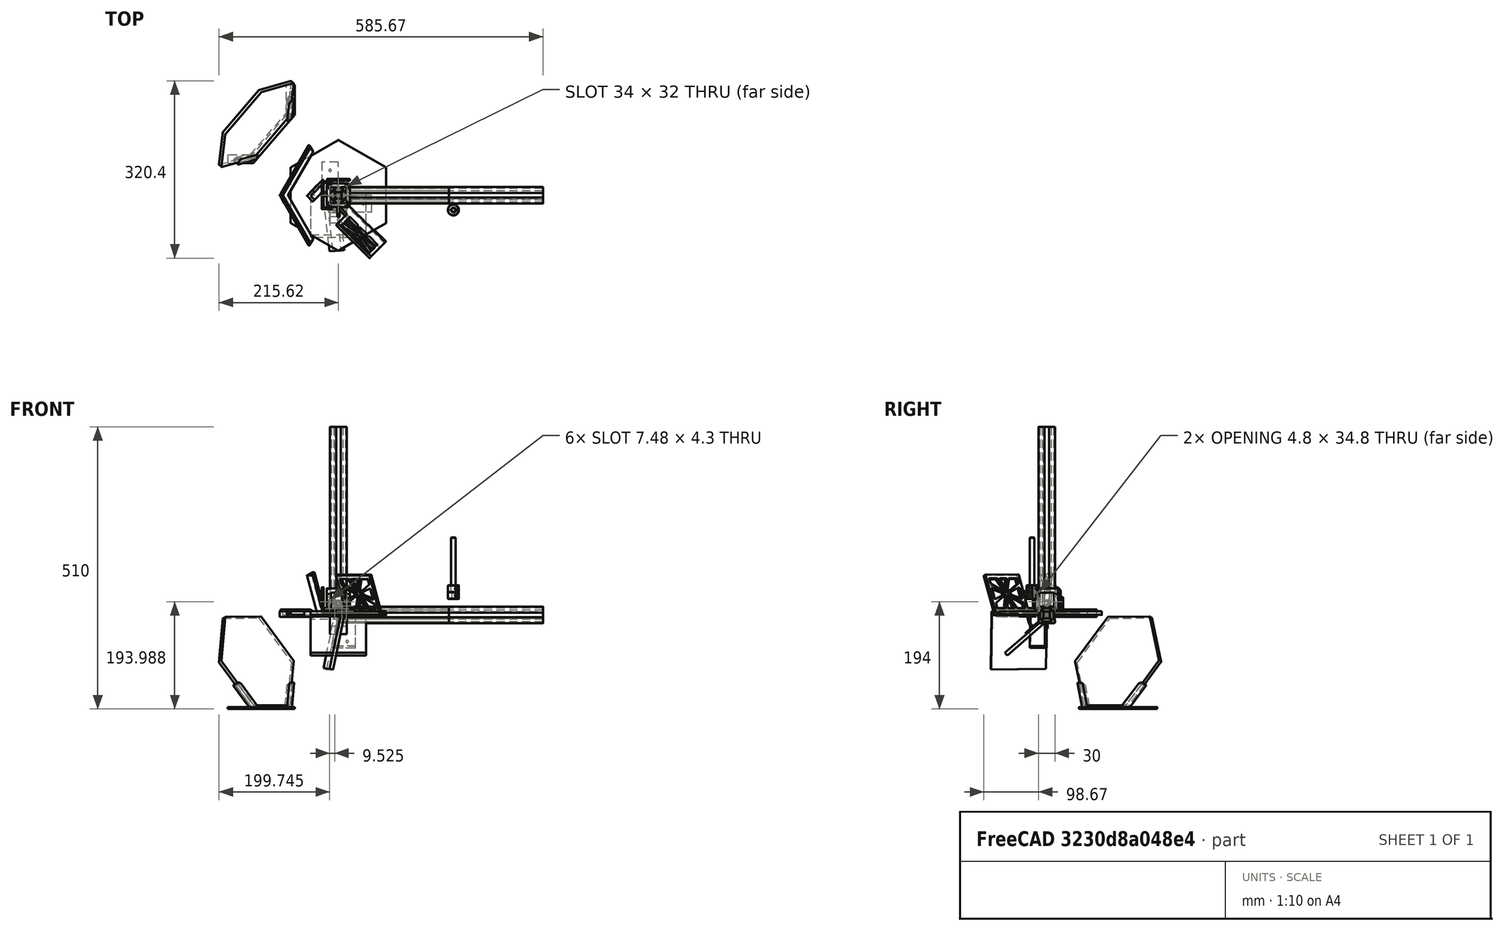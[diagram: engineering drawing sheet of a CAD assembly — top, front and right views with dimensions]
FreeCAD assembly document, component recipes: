
FREECAD ASSEMBLY — COMPONENT RECIPES ("frame")

This assembly document has 14 components, labeled P0..P13 below (a component is one placed body or linked part). 6 of them carry a construction recipe — the FreeCAD feature program that regenerates the part from scratch, quoted from this document or its linked companion documents; the rest are supplied as boundary geometry only. No exploded tour is included for this assembly.
COMPONENT P0 — geometry summary ("Extrusion"; no construction recipe available for this part):
  bounding box: 200.0 x 30.0 x 30.0 mm
  tessellated surface: 1,244 triangles
  volume: 87146 mm^3 (48% of its bounding box)
  symmetry: 4-fold rotationally symmetric about the x axis; 2-fold rotationally symmetric about the y axis; 2-fold rotationally symmetric about the z axis; mirror-symmetric across its x mid-plane, y mid-plane, z mid-plane
COMPONENT P1 — geometry summary ("Rubik's Cube"; no construction recipe available for this part):
  bounding box: 55.9 x 55.9 x 55.9 mm
  tessellated surface: 12 triangles
  volume: 174489 mm^3 (100% of its bounding box)
  symmetry: 4-fold rotationally symmetric about the x axis; 4-fold rotationally symmetric about the y axis; 4-fold rotationally symmetric about the z axis; mirror-symmetric across its x mid-plane, y mid-plane, z mid-plane
COMPONENT P2 — geometry summary ("Frame"; no construction recipe available for this part):
  bounding box: 503.7 x 446.7 x 440.0 mm
  tessellated surface: 211,220 triangles
  volume: 3022146 mm^3 (3% of its bounding box)
COMPONENT P3 — geometry summary ("Motor mount"; no construction recipe available for this part):
  bounding box: 74.0 x 64.2 x 51.2 mm
  tessellated surface: 18,230 triangles
  volume: 96011 mm^3 (40% of its bounding box)
COMPONENT P4 — geometry summary ("Extrusion 3"; no construction recipe available for this part):
  bounding box: 370.0 x 30.0 x 30.0 mm
  tessellated surface: 1,244 triangles
  volume: 161220 mm^3 (48% of its bounding box)
  symmetry: 4-fold rotationally symmetric about the x axis; 2-fold rotationally symmetric about the y axis; 2-fold rotationally symmetric about the z axis; mirror-symmetric across its x mid-plane, y mid-plane, z mid-plane
COMPONENT P5 — geometry summary ("Extrusion 2"; no construction recipe available for this part):
  bounding box: 200.0 x 30.0 x 30.0 mm
  tessellated surface: 1,244 triangles
  volume: 87146 mm^3 (48% of its bounding box)
  symmetry: 4-fold rotationally symmetric about the x axis; 2-fold rotationally symmetric about the y axis; 2-fold rotationally symmetric about the z axis; mirror-symmetric across its x mid-plane, y mid-plane, z mid-plane
COMPONENT P6 — geometry summary ("Extrusion 4"; no construction recipe available for this part):
  bounding box: 340.0 x 30.0 x 30.0 mm
  tessellated surface: 1,244 triangles
  volume: 148148 mm^3 (48% of its bounding box)
  symmetry: 2-fold rotationally symmetric about the x axis; 2-fold rotationally symmetric about the y axis; 4-fold rotationally symmetric about the z axis; mirror-symmetric across its x mid-plane, y mid-plane, z mid-plane
COMPONENT P7 — geometry summary ("Gripper"; no construction recipe available for this part):
  bounding box: 120.1 x 20.0 x 20.0 mm
  tessellated surface: 12,940 triangles
  volume: 14795 mm^3 (31% of its bounding box)
COMPONENT P8 — recipe-attached ("Mirror", modeled in this document).
Construction recipe (the document's own serialized feature program — sketch geometry with constraints, then the solid features built on it; lengths are millimeters unless a unit is written):

FEATURE [Sketcher::SketchObject] Sketch
  ArcFitTolerance = 1e-06
  AttachmentSupport = -> [XY_Plane011]
  ExternalTypes = [0]
  FullyConstrained = true
  MakeInternals = false
  MapMode = 5
  _ExternalGeoVersion = 0
  expr: Constraints[19] = Spreadsheet.H7
  sketch-geometry (7):
    g0: LineSegment StartX=-50 StartY=86.6025 StartZ=0 EndX=-100 EndY=0 EndZ=0
    g1: LineSegment StartX=-100 StartY=0 StartZ=0 EndX=-50 EndY=-86.6025 EndZ=0
    g2: LineSegment StartX=-50 StartY=-86.6025 StartZ=0 EndX=50 EndY=-86.6025 EndZ=0
    g3: LineSegment StartX=50 StartY=-86.6025 StartZ=0 EndX=100 EndY=-1.42e-14 EndZ=0
    g4: LineSegment StartX=100 StartY=-1.42e-14 StartZ=0 EndX=50 EndY=86.6025 EndZ=0
    g5: LineSegment StartX=50 StartY=86.6025 StartZ=0 EndX=-50 EndY=86.6025 EndZ=0
    g6: Circle [constr] CenterX=0 CenterY=0 CenterZ=0 NormalX=0 NormalY=0 NormalZ=1 AngleXU=0 Radius=100
  constraints (16):
    c: Coincident(g0,g1)
    c: Coincident(g1,g2)
    c: Coincident(g2,g3)
    c: Coincident(g3,g4)
    c: Coincident(g4,g5)
    c: Coincident(g5,g0)
    c: Equal(g0, g1-g5) x5
    c: PointOnObject(g0,g6)
    c: PointOnObject(g1,g6)
    c: PointOnObject(g2,g6)
    c: PointOnObject(g3,g6)
    c: PointOnObject(g4,g6)
    c: PointOnObject(g5,g6)
    c: Coincident(g6,g-1)
    c: Horizontal(g5)
    c: Diameter(g6) = 200
FEATURE [PartDesign::Pad] Pad001
  Direction = (0,0,1)
  Length = 6.35
  Length2 = 10
  Profile = -> Sketch
  ReferenceAxis = -> Sketch [N_Axis]
  Refine = true
  SideType = 0
  Suppressed = false
  Type = 0
  Type2 = 0
  expr: Length = Spreadsheet.H1
FEATURE [PartDesign::Fillet] Fillet001
  Base = -> Pad001 [Edge5,Edge8,Edge11,Edge14,Edge2,Edge1]
  BaseFeature = -> Pad001
  Radius = 1
  Refine = true
  SupportTransform = false
  Suppressed = false
  UseAllEdges = false
FEATURE [PartDesign::Body] Body001
  AllowCompound = false
  Group = -> [Pad001,Sketch,Fillet001]
  Origin = -> Origin011
  Placement = pos=(0,0,0) rot=(0,0,1;0.523599rad)
  Tip = -> Fillet001
COMPONENT P9 — recipe-attached ("Mirror frame", modeled in this document).
Construction recipe (the document's own serialized feature program — sketch geometry with constraints, then the solid features built on it; lengths are millimeters unless a unit is written):

FEATURE [Sketcher::SketchObject] Sketch002
  ArcFitTolerance = 1e-06
  AttachmentSupport = -> [XY_Plane013]
  ExternalTypes = [0]
  FullyConstrained = true
  MakeInternals = false
  MapMode = 5
  _ExternalGeoVersion = 0
  expr: Constraints[19] = Spreadsheet.H7 + Spreadsheet.H6
  expr: Constraints[34] = Spreadsheet.H3
  sketch-geometry (13):
    g0: LineSegment [constr] StartX=50.125 StartY=-86.819 StartZ=0 EndX=100.25 EndY=-5.684e-13 EndZ=0
    g1: LineSegment [constr] StartX=100.25 StartY=-5.684e-13 StartZ=0 EndX=50.125 EndY=86.819 EndZ=0
    g2: LineSegment [constr] StartX=50.125 StartY=86.819 StartZ=0 EndX=-50.125 EndY=86.819 EndZ=0
    g3: LineSegment StartX=-50.125 StartY=86.819 StartZ=0 EndX=-100.25 EndY=1.99e-13 EndZ=0
    g4: LineSegment StartX=-100.25 StartY=1.99e-13 StartZ=0 EndX=-50.125 EndY=-86.819 EndZ=0
    g5: LineSegment [constr] StartX=-50.125 StartY=-86.819 StartZ=0 EndX=50.125 EndY=-86.819 EndZ=0
    g6: Circle [constr] CenterX=0 CenterY=0 CenterZ=0 NormalX=0 NormalY=0 NormalZ=1 AngleXU=0 Radius=100.25
    g7: LineSegment [constr] StartX=0 StartY=0 StartZ=0 EndX=-50.125 EndY=86.819 EndZ=0
    g8: LineSegment [constr] StartX=0 StartY=0 StartZ=0 EndX=-50.125 EndY=-86.819 EndZ=0
    g9: LineSegment StartX=-50.125 StartY=-86.819 StartZ=0 EndX=-45.5062 EndY=-78.819 EndZ=0
    g10: LineSegment StartX=-50.125 StartY=86.819 StartZ=0 EndX=-45.5062 EndY=78.819 EndZ=0
    g11: LineSegment StartX=-45.5062 StartY=78.819 StartZ=0 EndX=-91.0124 EndY=0 EndZ=0
    g12: LineSegment StartX=-91.0124 StartY=0 StartZ=0 EndX=-45.5062 EndY=-78.819 EndZ=0
  constraints (31):
    c: Coincident(g0,g1)
    c: Coincident(g1,g2)
    c: Coincident(g2,g3)
    c: Coincident(g3,g4)
    c: Coincident(g4,g5)
    c: Coincident(g5,g0)
    c: Equal(g0, g1-g5) x5
    c: PointOnObject(g0,g6)
    c: PointOnObject(g1,g6)
    c: PointOnObject(g2,g6)
    c: PointOnObject(g3,g6)
    c: PointOnObject(g4,g6)
    c: PointOnObject(g5,g6)
    c: Coincident(g6,g-1)
    c: Horizontal(g2)
    c: DistanceX(g3,g0) = 200.5
    c: Coincident(g7,g6)
    c: Coincident(g7,g2)
    c: Coincident(g8,g6)
    c: Coincident(g8,g4)
    c: Coincident(g9,g4)
    c: PointOnObject(g9,g8)
    c: Coincident(g10,g2)
    c: PointOnObject(g10,g7)
    c: Coincident(g11,g10)
    c: PointOnObject(g11,g-1)
    c: Coincident(g12,g11)
    c: Coincident(g12,g9)
    c: Parallel(g3,g11)
    c: Parallel(g12,g4)
    c: Distance(g11,g3) = 8
FEATURE [PartDesign::Pad] Pad002
  Direction = (0,0,1)
  Length = 3
  Length2 = 10
  Profile = -> Sketch002
  ReferenceAxis = -> Sketch002 [N_Axis]
  Refine = true
  SideType = 0
  Suppressed = false
  Type = 0
  Type2 = 0
  expr: Length = Spreadsheet.H2
FEATURE [Sketcher::SketchObject] Sketch003  label="Sketch006"
  ArcFitTolerance = 1e-06
  AttachmentSupport = -> [XY_Plane013]
  ExternalTypes = [0]
  FullyConstrained = true
  MakeInternals = false
  MapMode = 5
  _ExternalGeoVersion = 0
  expr: Constraints[19] = Spreadsheet.H7 + Spreadsheet.H6
  expr: Constraints[34] = Spreadsheet.H4
  sketch-geometry (13):
    g0: LineSegment [constr] StartX=50.125 StartY=-86.819 StartZ=0 EndX=100.25 EndY=-5.542e-13 EndZ=0
    g1: LineSegment [constr] StartX=100.25 StartY=-5.542e-13 StartZ=0 EndX=50.125 EndY=86.819 EndZ=0
    g2: LineSegment [constr] StartX=50.125 StartY=86.819 StartZ=0 EndX=-50.125 EndY=86.819 EndZ=0
    g3: LineSegment StartX=-50.125 StartY=86.819 StartZ=0 EndX=-100.25 EndY=1.705e-13 EndZ=0
    g4: LineSegment StartX=-100.25 StartY=1.705e-13 StartZ=0 EndX=-50.125 EndY=-86.819 EndZ=0
    g5: LineSegment [constr] StartX=-50.125 StartY=-86.819 StartZ=0 EndX=50.125 EndY=-86.819 EndZ=0
    g6: Circle [constr] CenterX=0 CenterY=0 CenterZ=0 NormalX=0 NormalY=0 NormalZ=1 AngleXU=0 Radius=100.25
    g7: LineSegment [constr] StartX=0 StartY=0 StartZ=0 EndX=-50.125 EndY=86.819 EndZ=0
    g8: LineSegment [constr] StartX=0 StartY=0 StartZ=0 EndX=-50.125 EndY=-86.819 EndZ=0
    g9: LineSegment StartX=-50.125 StartY=-86.819 StartZ=0 EndX=-53.0118 EndY=-91.819 EndZ=0
    g10: LineSegment StartX=-50.125 StartY=86.819 StartZ=0 EndX=-53.0118 EndY=91.819 EndZ=0
    g11: LineSegment StartX=-53.0118 StartY=91.819 StartZ=0 EndX=-106.024 EndY=0 EndZ=0
    g12: LineSegment StartX=-106.024 StartY=0 StartZ=0 EndX=-53.0118 EndY=-91.819 EndZ=0
  constraints (31):
    c: Coincident(g0,g1)
    c: Coincident(g1,g2)
    c: Coincident(g2,g3)
    c: Coincident(g3,g4)
    c: Coincident(g4,g5)
    c: Coincident(g5,g0)
    c: Equal(g0, g1-g5) x5
    c: PointOnObject(g0,g6)
    c: PointOnObject(g1,g6)
    c: PointOnObject(g2,g6)
    c: PointOnObject(g3,g6)
    c: PointOnObject(g4,g6)
    c: PointOnObject(g5,g6)
    c: Coincident(g6,g-1)
    c: Horizontal(g2)
    c: DistanceX(g3,g0) = 200.5
    c: Coincident(g7,g6)
    c: Coincident(g7,g2)
    c: Coincident(g8,g6)
    c: Coincident(g8,g4)
    c: Coincident(g9,g4)
    c: PointOnObject(g9,g8)
    c: Coincident(g10,g2)
    c: PointOnObject(g10,g7)
    c: Coincident(g11,g10)
    c: PointOnObject(g11,g-1)
    c: Coincident(g12,g11)
    c: Coincident(g12,g9)
    c: Parallel(g3,g11)
    c: Parallel(g12,g4)
    c: Distance(g3,g11) = 5
FEATURE [PartDesign::Pad] Pad003
  BaseFeature = -> Pad002
  Direction = (0,0,1)
  Length = 10.35
  Length2 = 10
  Profile = -> Sketch003
  ReferenceAxis = -> Sketch003 [N_Axis]
  Refine = true
  SideType = 0
  Suppressed = false
  Type = 0
  Type2 = 0
  expr: Length = Spreadsheet.H5
FEATURE [Sketcher::SketchObject] Sketch004  label="Sketch007"
  ArcFitTolerance = 1e-06
  AttachmentSupport = -> [XZ_Plane014]
  ExternalTypes = [0]
  FullyConstrained = true
  MakeInternals = false
  MapMode = 5
  Placement = pos=(0,0,0) rot=(1,0,0;1.5708rad)
  _ExternalGeoVersion = 0
  expr: Constraints[16] = Spreadsheet.H9
  expr: Constraints[17] = Spreadsheet.H12
  expr: Constraints[18] = Spreadsheet.H1 + Spreadsheet.H6
  expr: Constraints[7] = Spreadsheet.H10 / 2
  expr: Constraints[9] = Spreadsheet.H11
  sketch-geometry (7):
    g0: LineSegment StartX=-103.5 StartY=6.85 StartZ=0 EndX=-104 EndY=8.35 EndZ=0
    g1: LineSegment StartX=-104 StartY=8.35 StartZ=0 EndX=-103.5 EndY=9.85 EndZ=0
    g2: LineSegment StartX=-103.5 StartY=9.85 StartZ=0 EndX=-101.5 EndY=9.85 EndZ=0
    g3: LineSegment StartX=-101.5 StartY=9.85 StartZ=0 EndX=-101 EndY=8.35 EndZ=0
    g4: LineSegment StartX=-101 StartY=8.35 StartZ=0 EndX=-101.5 EndY=6.85 EndZ=0
    g5: LineSegment StartX=-101.5 StartY=6.85 StartZ=0 EndX=-103.5 EndY=6.85 EndZ=0
    g6: LineSegment [constr] StartX=-102.5 StartY=9.85 StartZ=0 EndX=-102.5 EndY=6.85 EndZ=0
  constraints (19):
    c: Coincident(g1,g0)
    c: Coincident(g2,g1)
    c: Coincident(g3,g2)
    c: Coincident(g5,g4)
    c: Coincident(g5,g0)
    c: Equal(g2,g5)
    c: Coincident(g3,g4)
    c: DistanceX(g0,g1) = 0.5
    c: Equal(g1,g0)
    c: DistanceX(g0,g3) = 3
    c: PointOnObject(g6,g2)
    c: Symmetric(g5,g5,g6)
    c: Vertical(g6)
    c: Symmetric(g1,g2,g6)
    c: Symmetric(g0,g3,g6)
    c: Horizontal(g5)
    c: DistanceY(g6,g6) = 3
    c: Distance(g-1,g6) = 102.5
    c: Distance(g-1,g5) = 6.85
FEATURE [Sketcher::SketchObject] Sketch005  label="Sketch008"
  ArcFitTolerance = 1e-06
  AttachmentSupport = -> [XY_Plane014]
  ExternalTypes = [0]
  FullyConstrained = true
  MakeInternals = false
  MapMode = 5
  _ExternalGeoVersion = 0
  expr: Constraints[4] = Spreadsheet.H7 / 1.5
  sketch-geometry (2):
    g0: LineSegment StartX=0 StartY=0 StartZ=0 EndX=66.6667 EndY=115.47 EndZ=0
    g1: LineSegment StartX=0 StartY=0 StartZ=0 EndX=66.6667 EndY=-115.47 EndZ=0
  constraints (5):
    c: Coincident(g0,g-1)
    c: Coincident(g1,g0)
    c: Symmetric(g0,g1,g-1)
    c: Angle(g1,g0) = 2.0944
    c: Distance(g1,g1) = 133.333
FEATURE [PartDesign::AdditivePipe] AdditivePipe
  AuxiliaryCurvilinear = true
  AuxiliarySpineTangent = false
  Binormal = (0,0,0)
  Mode = 0
  Placement = pos=(0,0,0) rot=(1,0,0;1.5708rad)
  Profile = -> Sketch004
  Refine = true
  Spine = -> Sketch005
  SpineTangent = false
  Suppressed = false
  Transformation = 0
  Transition = 0
FEATURE [Sketcher::SketchObject] Sketch006  label="Sketch009"
  ArcFitTolerance = 1e-06
  AttachmentSupport = -> [XY_Plane014]
  ExternalTypes = [0]
  FullyConstrained = true
  MakeInternals = false
  MapMode = 5
  _ExternalGeoVersion = 0
  expr: Constraints[18] = Spreadsheet.H7 * 1.5
  expr: Constraints[34] = Spreadsheet.H7
  sketch-geometry (13):
    g0: LineSegment [constr] StartX=75 StartY=-129.904 StartZ=0 EndX=150 EndY=0 EndZ=0
    g1: LineSegment [constr] StartX=150 StartY=0 StartZ=0 EndX=75 EndY=129.904 EndZ=0
    g2: LineSegment [constr] StartX=75 StartY=129.904 StartZ=0 EndX=-75 EndY=129.904 EndZ=0
    g3: LineSegment [constr] StartX=-75 StartY=129.904 StartZ=0 EndX=-150 EndY=-2.84e-14 EndZ=0
    g4: LineSegment [constr] StartX=-150 StartY=-2.84e-14 StartZ=0 EndX=-75 EndY=-129.904 EndZ=0
    g5: LineSegment [constr] StartX=-75 StartY=-129.904 StartZ=0 EndX=75 EndY=-129.904 EndZ=0
    g6: Circle [constr] CenterX=0 CenterY=0 CenterZ=0 NormalX=0 NormalY=0 NormalZ=1 AngleXU=0 Radius=150
    g7: LineSegment StartX=0 StartY=0 StartZ=0 EndX=-115.47 EndY=200 EndZ=0
    g8: LineSegment StartX=0 StartY=0 StartZ=0 EndX=-115.47 EndY=-200 EndZ=0
    g9: LineSegment StartX=-115.47 StartY=-200 StartZ=0 EndX=34.5299 EndY=-200 EndZ=0
    g10: LineSegment StartX=34.5299 StartY=-200 StartZ=0 EndX=150 EndY=0 EndZ=0
    g11: LineSegment StartX=-115.47 StartY=200 StartZ=0 EndX=34.5299 EndY=200 EndZ=0
    g12: LineSegment StartX=34.5299 StartY=200 StartZ=0 EndX=150 EndY=0 EndZ=0
  constraints (31):
    c: Coincident(g0,g1)
    c: Coincident(g1,g2)
    c: Coincident(g2,g3)
    c: Coincident(g3,g4)
    c: Coincident(g4,g5)
    c: Coincident(g5,g0)
    c: Equal(g0, g1-g5) x5
    c: PointOnObject(g0,g6)
    c: PointOnObject(g1,g6)
    c: PointOnObject(g3,g6)
    c: PointOnObject(g4,g6)
    c: PointOnObject(g5,g6)
    c: Coincident(g6,g-1)
    c: Horizontal(g2)
    c: Diameter(g6) = 300
    c: Coincident(g7,g6)
    c: Coincident(g8,g6)
    c: PointOnObject(g2,g7)
    c: PointOnObject(g2,g6)
    c: Coincident(g9,g8)
    c: Coincident(g10,g9)
    c: Coincident(g10,g0)
    c: Coincident(g12,g11)
    c: Coincident(g12,g0)
    c: Horizontal(g11)
    c: Horizontal(g9)
    c: Coincident(g11,g7)
    c: Parallel(g7,g12)
    c: Parallel(g8,g10)
    c: Symmetric(g7,g8,g-1)
    c: DistanceY(g7,g7) = 200
FEATURE [PartDesign::Pocket] Pocket
  BaseFeature = -> AdditivePipe
  Direction = (0,0,-1)
  Length = 100
  Length2 = 5
  Placement = pos=(0,0,0) rot=(1,0,0;1.5708rad)
  Profile = -> Sketch006
  ReferenceAxis = -> Sketch006 [N_Axis]
  Refine = true
  Reversed = true
  SideType = 0
  Suppressed = false
  Type = 0
  Type2 = 0
FEATURE [PartDesign::Fillet] Fillet002
  Base = -> Pocket [Edge12,Edge2,Edge28,Edge19]
  BaseFeature = -> Pocket
  Placement = pos=(0,0,0) rot=(1,0,0;1.5708rad)
  Radius = 1
  Refine = true
  SupportTransform = false
  Suppressed = false
  UseAllEdges = false
FEATURE [PartDesign::Body] Body003
  AllowCompound = false
  Group = -> [Sketch004,Sketch005,AdditivePipe,Sketch006,Pocket,Fillet002]
  Origin = -> Origin014
  Tip = -> Fillet002
FEATURE [PartDesign::Boolean] Boolean
  BaseFeature = -> Pad003
  Group = -> [Binder]
  Refine = true
  Suppressed = false
  Type = 0
FEATURE [Sketcher::SketchObject] Sketch007  label="Sketch010"
  ArcFitTolerance = 1e-06
  AttachmentSupport = -> [XY_Plane013]
  ExternalTypes = [0]
  FullyConstrained = true
  MakeInternals = false
  MapMode = 5
  _ExternalGeoVersion = 0
  expr: Constraints[19] = Spreadsheet.H7 + Spreadsheet.H6
  expr: Constraints[36] = Spreadsheet.H14
  expr: Constraints[37] = Spreadsheet.H14
  expr: Constraints[52] = Spreadsheet.H4
  sketch-geometry (19):
    g0: LineSegment [constr] StartX=50.125 StartY=86.819 StartZ=0 EndX=-50.125 EndY=86.819 EndZ=0
    g1: LineSegment [constr] StartX=-50.125 StartY=86.819 StartZ=0 EndX=-100.25 EndY=0 EndZ=0
    g2: LineSegment [constr] StartX=-100.25 StartY=0 StartZ=0 EndX=-50.125 EndY=-86.819 EndZ=0
    g3: LineSegment [constr] StartX=-50.125 StartY=-86.819 StartZ=0 EndX=50.125 EndY=-86.819 EndZ=0
    g4: LineSegment [constr] StartX=50.125 StartY=-86.819 StartZ=0 EndX=100.25 EndY=-1.42e-14 EndZ=0
    g5: LineSegment [constr] StartX=100.25 StartY=-1.42e-14 StartZ=0 EndX=50.125 EndY=86.819 EndZ=0
    g6: Circle [constr] CenterX=0 CenterY=0 CenterZ=0 NormalX=0 NormalY=0 NormalZ=1 AngleXU=0 Radius=100.25
    g7: LineSegment [constr] StartX=0 StartY=0 StartZ=0 EndX=-53.0118 EndY=91.819 EndZ=0
    g8: LineSegment [constr] StartX=1.588e-13 StartY=0 StartZ=0 EndX=-53.0118 EndY=-91.819 EndZ=0
    g9: LineSegment [constr] StartX=-53.0118 StartY=91.819 StartZ=0 EndX=-106.024 EndY=0 EndZ=0
    g10: LineSegment [constr] StartX=-106.024 StartY=0 StartZ=0 EndX=-53.0118 EndY=-91.819 EndZ=0
    g11: LineSegment StartX=-61.9551 StartY=76.3287 StartZ=0 EndX=-57.625 EndY=73.8287 EndZ=0
    g12: LineSegment StartX=-97.0801 StartY=15.4904 StartZ=0 EndX=-92.75 EndY=12.9904 EndZ=0
    g13: LineSegment StartX=-97.0801 StartY=-15.4904 StartZ=0 EndX=-92.75 EndY=-12.9904 EndZ=0
    g14: LineSegment StartX=-61.9551 StartY=-76.3287 StartZ=0 EndX=-57.625 EndY=-73.8287 EndZ=0
    g15: LineSegment StartX=-57.625 StartY=73.8287 StartZ=0 EndX=-92.75 EndY=12.9904 EndZ=0
    g16: LineSegment StartX=-97.0801 StartY=15.4904 StartZ=0 EndX=-61.9551 EndY=76.3287 EndZ=0
    g17: LineSegment StartX=-92.75 StartY=-12.9904 StartZ=0 EndX=-57.625 EndY=-73.8287 EndZ=0
    g18: LineSegment StartX=-61.9551 StartY=-76.3287 StartZ=0 EndX=-97.0801 EndY=-15.4904 EndZ=0
  constraints (49):
    c: Coincident(g0,g1)
    c: Coincident(g1,g2)
    c: Coincident(g2,g3)
    c: Coincident(g3,g4)
    c: Coincident(g4,g5)
    c: Coincident(g5,g0)
    c: Equal(g0, g1-g5) x5
    c: PointOnObject(g0,g6)
    c: PointOnObject(g1,g6)
    c: PointOnObject(g2,g6)
    c: PointOnObject(g3,g6)
    c: PointOnObject(g4,g6)
    c: PointOnObject(g5,g6)
    c: Coincident(g6,g-1)
    c: Horizontal(g0)
    c: Diameter(g6) = 200.5
    c: Coincident(g7,g6)
    c: PointOnObject(g8,g-1)
    c: PointOnObject(g2,g8)
    c: PointOnObject(g0,g7)
    c: Symmetric(g7,g8,g-1)
    c: Coincident(g9,g7)
    c: PointOnObject(g9,g-1)
    c: Coincident(g10,g9)
    c: Coincident(g10,g8)
    c: Parallel(g10,g2)
    c: PointOnObject(g11,g9)
    c: PointOnObject(g11,g1)
    c: PointOnObject(g12,g9)
    c: PointOnObject(g12,g1)
    c: Perpendicular(g11,g9)
    c: Perpendicular(g12,g9)
    c: Distance(g0,g11) = 15
    c: Distance(g12,g1) = 15
    c: PointOnObject(g13,g10)
    c: PointOnObject(g14,g10)
    c: Perpendicular(g13,g2)
    c: Perpendicular(g14,g2)
    c: Symmetric(g12,g13,g-1)
    c: Symmetric(g14,g11,g-1)
    c: Coincident(g15,g11)
    c: Coincident(g15,g12)
    c: Coincident(g16,g12)
    c: Coincident(g16,g11)
    c: Coincident(g17,g13)
    c: Coincident(g17,g14)
    c: Coincident(g18,g14)
    c: Coincident(g18,g13)
    c: Distance(g1,g9) = 5
FEATURE [PartDesign::Pocket] Pocket001
  BaseFeature = -> Boolean
  Direction = (0,0,-1)
  Length = 100
  Length2 = 5
  Profile = -> Sketch007
  ReferenceAxis = -> Sketch007 [N_Axis]
  Refine = true
  Reversed = true
  SideType = 0
  Suppressed = false
  Type = 0
  Type2 = 0
FEATURE [Sketcher::SketchObject] Sketch008  label="Sketch011"
  ArcFitTolerance = 1e-06
  AttachmentSupport = -> [XY_Plane013]
  ExternalTypes = [0]
  FullyConstrained = true
  MakeInternals = false
  MapMode = 5
  _ExternalGeoVersion = 0
  expr: Constraints[19] = Spreadsheet.H7 + Spreadsheet.H6
  expr: Constraints[23] = Spreadsheet.H4
  expr: Constraints[33] = Spreadsheet.H4
  expr: Constraints[34] = Spreadsheet.H19
  sketch-geometry (15):
    g0: LineSegment [constr] StartX=50.125 StartY=86.819 StartZ=0 EndX=-50.125 EndY=86.819 EndZ=0
    g1: LineSegment [constr] StartX=-50.125 StartY=86.819 StartZ=0 EndX=-100.25 EndY=0 EndZ=0
    g2: LineSegment [constr] StartX=-100.25 StartY=0 StartZ=0 EndX=-50.125 EndY=-86.819 EndZ=0
    g3: LineSegment [constr] StartX=-50.125 StartY=-86.819 StartZ=0 EndX=50.125 EndY=-86.819 EndZ=0
    g4: LineSegment [constr] StartX=50.125 StartY=-86.819 StartZ=0 EndX=100.25 EndY=0 EndZ=0
    g5: LineSegment [constr] StartX=100.25 StartY=0 StartZ=0 EndX=50.125 EndY=86.819 EndZ=0
    g6: Circle [constr] CenterX=0 CenterY=0 CenterZ=0 NormalX=0 NormalY=0 NormalZ=1 AngleXU=0 Radius=100.25
    g7: LineSegment StartX=-88.3301 StartY=-30.6458 StartZ=0 EndX=-90.8301 EndY=-26.3157 EndZ=0
    g8: LineSegment StartX=-90.8301 StartY=-26.3157 StartZ=0 EndX=-86.5 EndY=-23.8157 EndZ=0
    g9: LineSegment StartX=-86.5 StartY=23.8157 StartZ=0 EndX=-84 EndY=28.1458 EndZ=0
    g10: LineSegment StartX=-84 StartY=28.1458 StartZ=0 EndX=-88.3301 EndY=30.6458 EndZ=0
    g11: LineSegment StartX=-88.3301 StartY=30.6458 StartZ=0 EndX=-90.8301 EndY=26.3157 EndZ=0
    g12: LineSegment StartX=-90.8301 StartY=26.3157 StartZ=0 EndX=-86.5 EndY=23.8157 EndZ=0
    g13: LineSegment StartX=-86.5 StartY=-23.8157 StartZ=0 EndX=-84 EndY=-28.1458 EndZ=0
    g14: LineSegment StartX=-88.3301 StartY=-30.6458 StartZ=0 EndX=-84 EndY=-28.1458 EndZ=0
  constraints (39):
    c: Coincident(g0,g1)
    c: Coincident(g1,g2)
    c: Coincident(g2,g3)
    c: Coincident(g3,g4)
    c: Coincident(g4,g5)
    c: Coincident(g5,g0)
    c: Equal(g0, g1-g5) x5
    c: PointOnObject(g0,g6)
    c: PointOnObject(g1,g6)
    c: PointOnObject(g2,g6)
    c: PointOnObject(g3,g6)
    c: PointOnObject(g4,g6)
    c: PointOnObject(g5,g6)
    c: Coincident(g6,g-1)
    c: Horizontal(g0)
    c: Diameter(g6) = 200.5
    c: PointOnObject(g8,g2)
    c: Coincident(g8,g7)
    c: Equal(g8,g7)
    c: Distance(g8,g8) = 5
    c: PointOnObject(g9,g1)
    c: Coincident(g10,g9)
    c: Coincident(g11,g10)
    c: Coincident(g12,g11)
    c: Coincident(g12,g9)
    c: Perpendicular(g10,g11)
    c: Perpendicular(g12,g11)
    c: Equal(g11,g10)
    c: Equal(g11,g12)
    c: Distance(g10,g10) = 5
    c: Distance(g1,g8) = 27.5
    c: Coincident(g13,g8)
    c: Coincident(g14,g7)
    c: Coincident(g14,g13)
    c: PointOnObject(g13,g2)
    c: Equal(g13,g7)
    c: Equal(g8,g14)
    c: Perpendicular(g7,g8)
    c: Symmetric(g9,g8,g-1)
FEATURE [PartDesign::Pad] Pad004
  BaseFeature = -> Pocket001
  Direction = (0,0,1)
  Length = 10.35
  Length2 = 10
  Profile = -> Sketch008
  ReferenceAxis = -> Sketch008 [N_Axis]
  Refine = true
  SideType = 0
  Suppressed = false
  Type = 0
  Type2 = 0
  expr: Length = Spreadsheet.H5
FEATURE [Sketcher::SketchObject] Sketch009  label="Sketch012"
  ArcFitTolerance = 1e-06
  AttachmentSupport = -> [XY_Plane013]
  ExternalTypes = [0]
  FullyConstrained = true
  MakeInternals = false
  MapMode = 5
  _ExternalGeoVersion = 0
  expr: Constraints[1] = Spreadsheet.H20 - Spreadsheet.H21
  expr: Constraints[22] = Spreadsheet.H7 + Spreadsheet.H6
  expr: Constraints[26] = Spreadsheet.H4 / 2
  expr: Constraints[27] = Spreadsheet.H18
  sketch-geometry (10):
    g0: Circle CenterX=-87.4151 CenterY=27.2308 CenterZ=0 NormalX=0 NormalY=0 NormalZ=1 AngleXU=0 Radius=1.25
    g1: Circle CenterX=-87.4151 CenterY=-27.2308 CenterZ=0 NormalX=0 NormalY=0 NormalZ=1 AngleXU=0 Radius=1.25
    g2: LineSegment [constr] StartX=-50.125 StartY=86.819 StartZ=0 EndX=-100.25 EndY=0 EndZ=0
    g3: LineSegment [constr] StartX=-100.25 StartY=0 StartZ=0 EndX=-50.125 EndY=-86.819 EndZ=0
    g4: LineSegment [constr] StartX=-50.125 StartY=-86.819 StartZ=0 EndX=50.125 EndY=-86.819 EndZ=0
    g5: LineSegment [constr] StartX=50.125 StartY=-86.819 StartZ=0 EndX=100.25 EndY=0 EndZ=0
    g6: LineSegment [constr] StartX=100.25 StartY=0 StartZ=0 EndX=50.125 EndY=86.819 EndZ=0
    g7: LineSegment [constr] StartX=50.125 StartY=86.819 StartZ=0 EndX=-50.125 EndY=86.819 EndZ=0
    g8: Circle [constr] CenterX=0 CenterY=0 CenterZ=0 NormalX=0 NormalY=0 NormalZ=1 AngleXU=0 Radius=100.25
    g9: LineSegment [constr] StartX=-87.4151 StartY=-27.2308 StartZ=0 EndX=-85.25 EndY=-25.9808 EndZ=0
  constraints (24):
    c: Equal(g0,g1)
    c: Diameter(g0) = 2.5
    c: Symmetric(g0,g1,g-1)
    c: Coincident(g2,g3)
    c: Coincident(g3,g4)
    c: Coincident(g4,g5)
    c: Coincident(g5,g6)
    c: Coincident(g6,g7)
    c: Coincident(g7,g2)
    c: Equal(g2, g3-g7) x5
    c: PointOnObject(g2,g8)
    c: PointOnObject(g3,g8)
    c: PointOnObject(g4,g8)
    c: PointOnObject(g5,g8)
    c: PointOnObject(g6,g8)
    c: PointOnObject(g7,g8)
    c: Coincident(g8,g-1)
    c: Horizontal(g7)
    c: Diameter(g8) = 200.5
    c: Coincident(g9,g1)
    c: PointOnObject(g9,g3)
    c: Perpendicular(g9,g3)
    c: Distance(g9,g9) = 2.5
    c: Distance(g9,g2) = 30
FEATURE [PartDesign::Pad] Pad005
  BaseFeature = -> Pad004
  Direction = (0,0,1)
  Length = 13.35
  Length2 = 10
  Profile = -> Sketch009
  ReferenceAxis = -> Sketch009 [N_Axis]
  Refine = true
  SideType = 0
  Suppressed = false
  Type = 0
  Type2 = 0
  expr: Length = Spreadsheet.K9
FEATURE [PartDesign::Plane] DatumPlane
  Length = 160.897
  MapMode = 1
  Placement = pos=(0,0,6.85) rot=(0,0,1;0rad)
  ResizeMode = 0
  Width = 212.388
  expr: .Placement.Base.z = Spreadsheet.H5 - Spreadsheet.H2 - Spreadsheet.H6
FEATURE [Sketcher::SketchObject] Sketch010  label="Sketch013"
  ArcFitTolerance = 1e-06
  AttachmentSupport = -> [DatumPlane]
  ExternalTypes = [0]
  FullyConstrained = true
  MakeInternals = false
  MapMode = 5
  Placement = pos=(0,0,6.85) rot=(0,0,1;0rad)
  _ExternalGeoVersion = 0
  expr: Constraints[19] = Spreadsheet.H7 + Spreadsheet.H6
  expr: Constraints[28] = Spreadsheet.H4
  expr: Constraints[40] = Spreadsheet.H3
  sketch-geometry (15):
    g0: LineSegment [constr] StartX=50.125 StartY=86.819 StartZ=0 EndX=-50.125 EndY=86.819 EndZ=0
    g1: LineSegment [constr] StartX=-50.125 StartY=86.819 StartZ=0 EndX=-100.25 EndY=0 EndZ=0
    g2: LineSegment [constr] StartX=-100.25 StartY=0 StartZ=0 EndX=-50.125 EndY=-86.819 EndZ=0
    g3: LineSegment [constr] StartX=-50.125 StartY=-86.819 StartZ=0 EndX=50.125 EndY=-86.819 EndZ=0
    g4: LineSegment [constr] StartX=50.125 StartY=-86.819 StartZ=0 EndX=100.25 EndY=0 EndZ=0
    g5: LineSegment [constr] StartX=100.25 StartY=0 StartZ=0 EndX=50.125 EndY=86.819 EndZ=0
    g6: Circle [constr] CenterX=0 CenterY=0 CenterZ=0 NormalX=0 NormalY=0 NormalZ=1 AngleXU=0 Radius=100.25
    g7: LineSegment [constr] StartX=0 StartY=0 StartZ=0 EndX=-53.0118 EndY=91.819 EndZ=0
    g8: LineSegment [constr] StartX=0 StartY=0 StartZ=0 EndX=-53.0118 EndY=-91.819 EndZ=0
    g9: LineSegment StartX=-53.0118 StartY=-91.819 StartZ=0 EndX=-106.024 EndY=0 EndZ=0
    g10: LineSegment StartX=-106.024 StartY=0 StartZ=0 EndX=-53.0118 EndY=91.819 EndZ=0
    g11: LineSegment StartX=-53.0118 StartY=91.819 StartZ=0 EndX=-45.5062 EndY=78.819 EndZ=0
    g12: LineSegment StartX=-53.0118 StartY=-91.819 StartZ=0 EndX=-45.5062 EndY=-78.819 EndZ=0
    g13: LineSegment StartX=-45.5062 StartY=-78.819 StartZ=0 EndX=-91.0124 EndY=0 EndZ=0
    g14: LineSegment StartX=-45.5062 StartY=78.819 StartZ=0 EndX=-91.0124 EndY=0 EndZ=0
  constraints (37):
    c: Coincident(g0,g1)
    c: Coincident(g1,g2)
    c: Coincident(g2,g3)
    c: Coincident(g3,g4)
    c: Coincident(g4,g5)
    c: Coincident(g5,g0)
    c: Equal(g0, g1-g5) x5
    c: PointOnObject(g0,g6)
    c: PointOnObject(g1,g6)
    c: PointOnObject(g2,g6)
    c: PointOnObject(g3,g6)
    c: PointOnObject(g4,g6)
    c: PointOnObject(g5,g6)
    c: Coincident(g6,g-1)
    c: Horizontal(g0)
    c: Diameter(g6) = 200.5
    c: Coincident(g7,g6)
    c: PointOnObject(g0,g7)
    c: Coincident(g8,g6)
    c: PointOnObject(g2,g8)
    c: Coincident(g9,g8)
    c: Coincident(g10,g9)
    c: Coincident(g10,g7)
    c: PointOnObject(g9,g-1)
    c: Distance(g0,g10) = 5
    c: Coincident(g11,g7)
    c: PointOnObject(g11,g7)
    c: Coincident(g12,g8)
    c: Coincident(g13,g12)
    c: PointOnObject(g13,g-1)
    c: Coincident(g14,g11)
    c: Coincident(g14,g13)
    c: Parallel(g10,g14)
    c: Parallel(g13,g9)
    c: Parallel(g2,g9)
    c: Symmetric(g11,g12,g-1)
    c: Distance(g14,g1) = 8
FEATURE [PartDesign::Pad] Pad006
  Direction = (0,0,1)
  Length = 3
  Length2 = 10
  Placement = pos=(0,0,6.85) rot=(0,0,1;0rad)
  Profile = -> Sketch010
  ReferenceAxis = -> Sketch010 [N_Axis]
  Refine = true
  SideType = 0
  Suppressed = false
  Type = 0
  Type2 = 0
  expr: Length = Spreadsheet.H11
FEATURE [PartDesign::Boolean] Boolean001
  BaseFeature = -> Pad006
  Group = -> [Binder001]
  Refine = true
  Suppressed = false
  Type = 1
FEATURE [PartDesign::Fillet] Fillet
  Base = -> Pad005 [Edge36,Edge37,Edge34,Edge33,Edge119,Edge120,Edge116,Edge117,Edge47,Edge45,Edge51,Edge53,Edge109,Edge110,Edge107,Edge106,Edge70,Edge71,Edge68,Edge67,Edge14,Edge15,Edge12,Edge11]
  BaseFeature = -> Pad005
  Radius = 0.5
  Refine = true
  SupportTransform = false
  Suppressed = false
  UseAllEdges = false
FEATURE [PartDesign::Fillet] Fillet004
  Base = -> Fillet [Edge146,Edge145,Edge159,Edge158,Edge148,Edge76,Edge128,Edge133,Edge130,Edge127,Edge124,Edge114,Edge112,Edge110,Edge109,Edge91,Edge94,Edge92,Edge97,Edge41,Edge43,Edge14,Edge11,Edge10]
  BaseFeature = -> Fillet
  Radius = 1
  Refine = true
  SupportTransform = false
  Suppressed = false
  UseAllEdges = false
FEATURE [PartDesign::Fillet] Fillet005
  Base = -> Fillet004 [Edge150,Edge184,Edge179,Edge185,Edge199,Edge155]
  BaseFeature = -> Fillet004
  Radius = 1
  Refine = true
  SupportTransform = false
  Suppressed = false
  UseAllEdges = false
FEATURE [PartDesign::Body] Body002
  AllowCompound = false
  Group = -> [Sketch002,Pad002,Sketch003,Pad003,Boolean,Sketch007,Pocket001,Sketch008,Pad004,Sketch009,Pad005,Fillet,Fillet004,Fillet005]
  Origin = -> Origin013
  Placement = pos=(0,0,-3.5) rot=(0,0,1;0rad)
  Tip = -> Fillet005
  expr: .Placement.Base.z = -Spreadsheet.H2 - Spreadsheet.H6
FEATURE [Sketcher::SketchObject] Sketch011  label="Sketch014"
  ArcFitTolerance = 1e-06
  AttachmentSupport = -> [DatumPlane]
  ExternalTypes = [0]
  FullyConstrained = true
  MakeInternals = false
  MapMode = 5
  Placement = pos=(0,0,6.85) rot=(0,0,1;0rad)
  _ExternalGeoVersion = 0
  expr: Constraints[17] = Spreadsheet.H7 + Spreadsheet.H6
  expr: Constraints[27] = Spreadsheet.H4
  expr: Constraints[28] = Spreadsheet.H16
  expr: Constraints[29] = Spreadsheet.H16
  sketch-geometry (15):
    g0: LineSegment [constr] StartX=50.125 StartY=86.819 StartZ=0 EndX=-50.125 EndY=86.819 EndZ=0
    g1: LineSegment [constr] StartX=-50.125 StartY=86.819 StartZ=0 EndX=-100.25 EndY=1.42e-14 EndZ=0
    g2: LineSegment [constr] StartX=-100.25 StartY=1.42e-14 StartZ=0 EndX=-50.125 EndY=-86.819 EndZ=0
    g3: LineSegment [constr] StartX=-50.125 StartY=-86.819 StartZ=0 EndX=50.125 EndY=-86.819 EndZ=0
    g4: LineSegment [constr] StartX=50.125 StartY=-86.819 StartZ=0 EndX=100.25 EndY=0 EndZ=0
    g5: LineSegment [constr] StartX=100.25 StartY=0 StartZ=0 EndX=50.125 EndY=86.819 EndZ=0
    g6: Circle [constr] CenterX=0 CenterY=0 CenterZ=0 NormalX=0 NormalY=0 NormalZ=1 AngleXU=0 Radius=100.25
    g7: LineSegment StartX=-87.75 StartY=21.6506 StartZ=0 EndX=-62.625 EndY=65.1684 EndZ=0
    g8: LineSegment StartX=-62.625 StartY=65.1684 StartZ=0 EndX=-66.9551 EndY=67.6684 EndZ=0
    g9: LineSegment StartX=-87.75 StartY=21.6506 StartZ=0 EndX=-92.0801 EndY=24.1506 EndZ=0
    g10: LineSegment StartX=-92.0801 StartY=24.1506 StartZ=0 EndX=-66.9551 EndY=67.6684 EndZ=0
    g11: LineSegment StartX=-87.75 StartY=-21.6506 StartZ=0 EndX=-62.625 EndY=-65.1684 EndZ=0
    g12: LineSegment StartX=-62.625 StartY=-65.1684 StartZ=0 EndX=-66.9551 EndY=-67.6684 EndZ=0
    g13: LineSegment StartX=-66.9551 StartY=-67.6684 StartZ=0 EndX=-92.0801 EndY=-24.1506 EndZ=0
    g14: LineSegment StartX=-92.0801 StartY=-24.1506 StartZ=0 EndX=-87.75 EndY=-21.6506 EndZ=0
  constraints (39):
    c: Coincident(g0,g1)
    c: Coincident(g1,g2)
    c: Coincident(g3,g4)
    c: Coincident(g4,g5)
    c: Coincident(g5,g0)
    c: Equal(g0, g1-g5) x5
    c: PointOnObject(g0,g6)
    c: PointOnObject(g1,g6)
    c: PointOnObject(g2,g6)
    c: PointOnObject(g3,g6)
    c: PointOnObject(g4,g6)
    c: PointOnObject(g5,g6)
    c: Horizontal(g0)
    c: Diameter(g6) = 200.5
    c: PointOnObject(g7,g1)
    c: PointOnObject(g7,g1)
    c: Coincident(g8,g7)
    c: Coincident(g9,g7)
    c: Coincident(g10,g9)
    c: Coincident(g10,g8)
    c: Equal(g8,g9)
    c: Perpendicular(g7,g8)
    c: Perpendicular(g7,g9)
    c: Distance(g8,g8) = 5
    c: Distance(g7,g0) = 25
    c: Distance(g1,g7) = 25
    c: PointOnObject(g11,g2)
    c: Coincident(g12,g11)
    c: Coincident(g13,g12)
    c: Coincident(g14,g11)
    c: Perpendicular(g11,g14)
    c: Perpendicular(g11,g12)
    c: Equal(g14,g9)
    c: Coincident(g14,g13)
    c: Perpendicular(g12,g13)
    c: Symmetric(g7,g11,g-1)
    c: Equal(g10,g13)
    c: Coincident(g2,g3)
    c: Coincident(g6,g-1)
FEATURE [PartDesign::Pad] Pad007
  BaseFeature = -> Boolean001
  Direction = (0,0,1)
  Length = 3
  Length2 = 10
  Profile = -> Sketch011
  ReferenceAxis = -> Sketch011 [N_Axis]
  Refine = true
  SideType = 0
  Suppressed = false
  Type = 0
  Type2 = 0
  expr: Length = Spreadsheet.H20
FEATURE [Sketcher::SketchObject] Sketch012  label="Sketch015"
  ArcFitTolerance = 1e-06
  AttachmentSupport = -> [DatumPlane]
  ExternalTypes = [0]
  FullyConstrained = true
  MakeInternals = false
  MapMode = 5
  Placement = pos=(0,0,6.85) rot=(0,0,1;0rad)
  _ExternalGeoVersion = 0
  expr: Constraints[19] = Spreadsheet.H7 + Spreadsheet.H6
  expr: Constraints[22] = Spreadsheet.H18
  expr: Constraints[23] = Spreadsheet.H4 / 2
  expr: Constraints[25] = Spreadsheet.H20
  expr: Constraints[36] = Spreadsheet.H23
  expr: Constraints[38] = Spreadsheet.I12
  sketch-geometry (14):
    g0: LineSegment [constr] StartX=50.125 StartY=86.819 StartZ=0 EndX=-50.125 EndY=86.819 EndZ=0
    g1: LineSegment [constr] StartX=-50.125 StartY=86.819 StartZ=0 EndX=-100.25 EndY=-1.42e-14 EndZ=0
    g2: LineSegment [constr] StartX=-100.25 StartY=-1.42e-14 StartZ=0 EndX=-50.125 EndY=-86.819 EndZ=0
    g3: LineSegment [constr] StartX=-50.125 StartY=-86.819 StartZ=0 EndX=50.125 EndY=-86.819 EndZ=0
    g4: LineSegment [constr] StartX=50.125 StartY=-86.819 StartZ=0 EndX=100.25 EndY=1.42e-14 EndZ=0
    g5: LineSegment [constr] StartX=100.25 StartY=1.42e-14 StartZ=0 EndX=50.125 EndY=86.819 EndZ=0
    g6: Circle [constr] CenterX=0 CenterY=0 CenterZ=0 NormalX=0 NormalY=0 NormalZ=1 AngleXU=0 Radius=100.25
    g7: LineSegment [constr] StartX=-65.125 StartY=60.8383 StartZ=0 EndX=-67.2901 EndY=62.0883 EndZ=0
    g8: Circle CenterX=-67.2901 CenterY=62.0883 CenterZ=0 NormalX=0 NormalY=0 NormalZ=1 AngleXU=0 Radius=1.5
    g9: Circle CenterX=-67.2901 CenterY=-62.0883 CenterZ=0 NormalX=0 NormalY=0 NormalZ=1 AngleXU=0 Radius=1.5
    g10: LineSegment StartX=-112.75 StartY=0.25 StartZ=0 EndX=-112.75 EndY=-0.25 EndZ=0
    g11: LineSegment StartX=-112.75 StartY=-0.25 StartZ=0 EndX=-102.75 EndY=-0.25 EndZ=0
    g12: LineSegment StartX=-102.75 StartY=-0.25 StartZ=0 EndX=-102.75 EndY=0.25 EndZ=0
    g13: LineSegment StartX=-102.75 StartY=0.25 StartZ=0 EndX=-112.75 EndY=0.25 EndZ=0
  constraints (35):
    c: Coincident(g0,g1)
    c: Coincident(g1,g2)
    c: Coincident(g2,g3)
    c: Coincident(g3,g4)
    c: Coincident(g4,g5)
    c: Coincident(g5,g0)
    c: Equal(g0, g1-g5) x5
    c: PointOnObject(g0,g6)
    c: PointOnObject(g1,g6)
    c: PointOnObject(g2,g6)
    c: PointOnObject(g3,g6)
    c: PointOnObject(g4,g6)
    c: PointOnObject(g5,g6)
    c: Coincident(g6,g-1)
    c: Horizontal(g0)
    c: Diameter(g6) = 200.5
    c: PointOnObject(g7,g1)
    c: Perpendicular(g1,g7)
    c: Distance(g0,g7) = 30
    c: Distance(g7,g7) = 2.5
    c: Coincident(g8,g7)
    c: Diameter(g8) = 3
    c: Symmetric(g7,g9,g-1)
    c: Equal(g8,g9)
    c: Coincident(g10,g11)
    c: Coincident(g11,g12)
    c: Coincident(g12,g13)
    c: Coincident(g13,g10)
    c: Vertical(g12)
    c: Horizontal(g11)
    c: Horizontal(g13)
    c: Symmetric(g10,g10,g-1)
    c: DistanceY(g10,g10) = 0.5
    c: DistanceX(g13,g13) = 10
    c: Distance(g1,g12) = 2.5
FEATURE [PartDesign::Pocket] Pocket002
  BaseFeature = -> Pad007
  Direction = (0,0,-1)
  Length = 100
  Length2 = 5
  Profile = -> Sketch012
  ReferenceAxis = -> Sketch012 [N_Axis]
  Refine = true
  Reversed = true
  SideType = 0
  Suppressed = false
  Type = 0
  Type2 = 0
FEATURE [Sketcher::SketchObject] Sketch013  label="Sketch016"
  ArcFitTolerance = 1e-06
  AttachmentSupport = -> [XZ_Plane015]
  ExternalTypes = [0]
  FullyConstrained = true
  MakeInternals = false
  MapMode = 5
  Placement = pos=(0,0,0) rot=(1,0,0;1.5708rad)
  _ExternalGeoVersion = 0
  expr: Constraints[3] = Spreadsheet.H9
  expr: Constraints[4] = Spreadsheet.H3 * 1 / cos(30)
  expr: Constraints[7] = Spreadsheet.H5 - Spreadsheet.H2 - Spreadsheet.H6
  expr: Constraints[8] = Spreadsheet.H7 / 2 + Spreadsheet.H6 / 2
  sketch-geometry (3):
    g0: LineSegment StartX=-91.0124 StartY=6.85 StartZ=0 EndX=-100.25 EndY=9.85 EndZ=0
    g1: LineSegment StartX=-100.25 StartY=9.85 StartZ=0 EndX=-91.0124 EndY=9.85 EndZ=0
    g2: LineSegment StartX=-91.0124 StartY=9.85 StartZ=0 EndX=-91.0124 EndY=6.85 EndZ=0
  constraints (9):
    c: Horizontal(g1)
    c: Coincident(g2,g0)
    c: Vertical(g2)
    c: DistanceY(g2,g2) = 3
    c: DistanceX(g1,g1) = 9.2376
    c: Coincident(g1,g2)
    c: Coincident(g0,g1)
    c: Distance(g0,g-1) = 6.85
    c: Distance(g0,g-2) = 100.25
FEATURE [PartDesign::SubtractivePipe] SubtractivePipe
  AuxiliaryCurvilinear = true
  AuxiliarySpineTangent = false
  BaseFeature = -> Pocket002
  Binormal = (0,0,0)
  Mode = 0
  Profile = -> Sketch013
  Refine = true
  Spine = -> Pocket002 [Edge36]
  SpineTangent = false
  Suppressed = false
  Transformation = 0
  Transition = 0
FEATURE [PartDesign::SubtractivePipe] SubtractivePipe001
  AuxiliaryCurvilinear = true
  AuxiliarySpineTangent = false
  BaseFeature = -> SubtractivePipe
  Binormal = (0,0,0)
  Mode = 0
  Profile = -> Sketch013
  Refine = true
  Spine = -> SubtractivePipe [Edge48]
  SpineTangent = false
  Suppressed = false
  Transformation = 0
  Transition = 0
FEATURE [PartDesign::Fillet] Fillet006
  Base = -> SubtractivePipe001 [Edge5,Edge61,Edge81,Edge80,Edge69,Edge68,Edge66]
  BaseFeature = -> SubtractivePipe001
  Radius = 1
  Refine = true
  SupportTransform = false
  Suppressed = false
  UseAllEdges = false
FEATURE [PartDesign::Body] Body004
  AllowCompound = true
  Group = -> [DatumPlane,Sketch010,Pad006,Boolean001,Sketch011,Pad007,Sketch012,Pocket002,Sketch013,SubtractivePipe,SubtractivePipe001,Fillet006]
  Origin = -> Origin015
  Tip = -> Fillet006
COMPONENT P10 — recipe-attached ("Mirror rails", modeled in this document).
Construction recipe (the document's own serialized feature program — sketch geometry with constraints, then the solid features built on it; lengths are millimeters unless a unit is written):

FEATURE [PartDesign::SubShapeBinder] Binder002
  BindCopyOnChange = 0
  BindMode = 0
  ClaimChildren = false
  Context = -> Part011 [Body005.Binder002.]
  Fuse = false
  MakeFace = true
  OffsetFill = false
  OffsetIntersection = false
  OffsetJoinType = 0
  OffsetOpenResult = false
  PartialLoad = false
  Placement = pos=(-150,130,-85) rot=(0.31254,0.821685,-0.476605;1.35525rad)
  Refine = true
  Relative = true
  Support = -> [Part009[Body001.]]
  _Version = 2
FEATURE [PartDesign::Plane] DatumPlane001
  Length = 270
  MapMode = 1
  Placement = pos=(0,0,-170) rot=(0,0,1;0rad)
  ResizeMode = 0
  Width = 270
  expr: .Placement.Base.z = -Spreadsheet.B14 + Spreadsheet.E1
FEATURE [Sketcher::SketchObject] Sketch014  label="Sketch017"
  ArcFitTolerance = 1e-06
  AttachmentSupport = -> [DatumPlane001]
  ExternalGeometry = -> [Binder002]
  ExternalTypes = [0]
  FullyConstrained = true
  MakeInternals = false
  MapMode = 5
  Placement = pos=(0,0,-170) rot=(0,0,1;0rad)
  _ExternalGeoVersion = 0
  expr: Constraints[31] = Spreadsheet.B14 - Spreadsheet.E2
  expr: Constraints[32] = Spreadsheet.B14 - Spreadsheet.E2
  expr: Constraints[43] = Spreadsheet.E2
  expr: Constraints[46] = Spreadsheet.H7 / 2 + Spreadsheet.H6
  sketch-geometry (18):
    g0: LineSegment StartX=-93.8844 StartY=200 StartZ=0 EndX=-78.8844 EndY=200 EndZ=0
    g1: LineSegment StartX=-200 StartY=72.9731 StartZ=0 EndX=-200 EndY=57.9731 EndZ=0
    g2: LineSegment StartX=-154.307 StartY=57.9731 StartZ=0 EndX=-78.8844 EndY=144.737 EndZ=0
    g3: LineSegment StartX=-159.818 StartY=72.9731 StartZ=0 EndX=-93.8844 EndY=148.821 EndZ=0
    g4: LineSegment StartX=-93.8844 StartY=148.821 StartZ=0 EndX=-93.8844 EndY=200 EndZ=0
    g5: LineSegment StartX=-78.8844 StartY=200 StartZ=0 EndX=-78.8844 EndY=144.737 EndZ=0
    g6: LineSegment StartX=-159.818 StartY=72.9731 StartZ=0 EndX=-200 EndY=72.9731 EndZ=0
    g7: LineSegment StartX=-200 StartY=57.9731 StartZ=0 EndX=-154.307 EndY=57.9731 EndZ=0
    g8: Circle CenterX=-185 CenterY=65.4731 CenterZ=0 NormalX=0 NormalY=0 NormalZ=1 AngleXU=0 Radius=2.2
    g9: Circle CenterX=-86.3844 CenterY=185 CenterZ=0 NormalX=0 NormalY=0 NormalZ=1 AngleXU=0 Radius=2.2
    g10: LineSegment [constr] StartX=-86.3844 StartY=185 StartZ=0 EndX=-93.8844 EndY=185 EndZ=0
    g11: LineSegment [constr] StartX=-86.3844 StartY=185 StartZ=0 EndX=-78.8844 EndY=185 EndZ=0
    g12: LineSegment [constr] StartX=-185 StartY=65.4731 StartZ=0 EndX=-185 EndY=72.9731 EndZ=0
    g13: LineSegment [constr] StartX=-185 StartY=65.4731 StartZ=0 EndX=-185 EndY=57.9731 EndZ=0
    g14: LineSegment [constr] StartX=0 StartY=0 StartZ=0 EndX=-116.596 EndY=101.355 EndZ=0
    g15: LineSegment [constr] StartX=-200 StartY=65.4731 StartZ=0 EndX=-185 EndY=65.4731 EndZ=0
    g16: LineSegment [constr] StartX=-86.3844 StartY=185 StartZ=0 EndX=-86.3844 EndY=200 EndZ=0
    g17: LineSegment [constr] StartX=-126.851 StartY=110.897 StartZ=0 EndX=-123.833 EndY=108.273 EndZ=0
  constraints (51):
    c: Horizontal(g0)
    c: Vertical(g1)
    c: Coincident(g4,g3)
    c: Coincident(g4,g0)
    c: Coincident(g5,g0)
    c: Coincident(g5,g2)
    c: Coincident(g6,g3)
    c: Coincident(g6,g1)
    c: Coincident(g7,g1)
    c: Coincident(g7,g2)
    c: Vertical(g4)
    c: Vertical(g5)
    c: Horizontal(g6)
    c: Horizontal(g7)
    c: Equal(g0,g1)
    c: Coincident(g10,g9)
    c: PointOnObject(g10,g4)
    c: Coincident(g11,g9)
    c: PointOnObject(g11,g5)
    c: Equal(g10,g11)
    c: Perpendicular(g10,g4)
    c: Perpendicular(g5,g11)
    c: Coincident(g12,g8)
    c: PointOnObject(g12,g6)
    c: Coincident(g13,g8)
    c: PointOnObject(g13,g7)
    c: Equal(g12,g13)
    c: Perpendicular(g6,g12)
    c: Perpendicular(g7,g13)
    c: Equal(g8,g9)
    c: Diameter(g8) = 4.4
    c: Distance(g8,g-2) = 185
    c: Distance(g9,g-1) = 185
    c: Coincident(g14,g-1)
    c: Symmetric(g2,g2,g14)
    c: Parallel(g3,g2)
    c: Perpendicular(g14,g2)
    c: DistanceX(g0,g0) = 15
    c: Symmetric(g1,g1,g15)
    c: Coincident(g15,g8)
    c: Coincident(g16,g9)
    c: Symmetric(g0,g0,g16)
    c: Equal(g16,g15)
    c: DistanceY(g16,g16) = 15
    c: Angle(g14,g-1) = 0.715585
    c: Distance(g2,g3) = 14
    c: Distance(g3,g3) = 100.5
    c: Symmetric(g3,g3,g17)
    c: PointOnObject(g17,g-3)
    c: Perpendicular(g17,g3)
    c: Distance(g17,g17) = 4
FEATURE [PartDesign::Pad] Pad008
  Direction = (0,0,1)
  Length = 3
  Length2 = 10
  Placement = pos=(0,0,-170) rot=(0,0,1;0rad)
  Profile = -> Sketch014
  ReferenceAxis = -> Sketch014 [N_Axis]
  Refine = true
  SideType = 0
  Suppressed = false
  Type = 0
  Type2 = 0
FEATURE [PartDesign::Plane] DatumPlane002
  AttachmentSupport = -> [Pad008]
  Length = 367.181
  MapMode = 7
  Placement = pos=(-159.818,72.9731,-167) rot=(0.884029,-0.330525,-0.330525;1.69375rad)
  ResizeMode = 0
  Width = 244.758
FEATURE [Sketcher::SketchObject] Sketch015  label="Sketch018"
  ArcFitTolerance = 1e-06
  AttachmentSupport = -> [DatumPlane002]
  ExternalTypes = [0]
  FullyConstrained = true
  MakeInternals = false
  MapMode = 5
  Placement = pos=(-159.818,72.9731,-167) rot=(0.884029,-0.330525,-0.330525;1.69375rad)
  _ExternalGeoVersion = 0
  sketch-geometry (1):
    g0: LineSegment StartX=0 StartY=0 StartZ=0 EndX=-70.3785 EndY=165.801 EndZ=0
  constraints (3):
    c: Coincident(g0,g-1)
    c: Angle(g0,g-1) = 1.16937
    c: Distance(g0,g0) = 180.12
FEATURE [PartDesign::Plane] DatumPlane003
  AttachmentSupport = -> [Sketch015]
  Length = 385.814
  MapMode = 7
  Placement = pos=(-159.818,72.9731,-167) rot=(0.90674,0.413225,0.084072;2.77674rad)
  ResizeMode = 0
  Width = 436.773
FEATURE [Sketcher::SketchObject] Sketch016  label="Sketch019"
  ArcFitTolerance = 1e-06
  AttachmentSupport = -> [DatumPlane003]
  ExternalTypes = [0]
  FullyConstrained = true
  MakeInternals = false
  MapMode = 5
  Placement = pos=(-159.818,72.9731,-167) rot=(0.90674,0.413225,0.084072;2.77674rad)
  _ExternalGeoVersion = 0
  expr: Constraints[17] = Spreadsheet.N1
  expr: Constraints[24] = Spreadsheet.N1
  expr: Constraints[26] = Spreadsheet.N2
  expr: Constraints[7] = Spreadsheet.H1 + Spreadsheet.H6
  sketch-geometry (10):
    g0: LineSegment StartX=0 StartY=3 StartZ=0 EndX=0 EndY=9.85 EndZ=0
    g1: LineSegment StartX=-3 StartY=0 StartZ=0 EndX=-3 EndY=12.85 EndZ=0
    g2: LineSegment StartX=0 StartY=9.85 StartZ=0 EndX=8 EndY=9.85 EndZ=0
    g3: LineSegment StartX=8 StartY=3 StartZ=0 EndX=0 EndY=3 EndZ=0
    g4: LineSegment StartX=-3 StartY=12.85 StartZ=0 EndX=0 EndY=12.85 EndZ=0
    g5: LineSegment StartX=0 StartY=12.85 StartZ=0 EndX=8 EndY=9.85 EndZ=0
    g6: LineSegment StartX=8 StartY=3 StartZ=0 EndX=9e-16 EndY=0 EndZ=0
    g7: LineSegment StartX=0 StartY=0 StartZ=0 EndX=-3 EndY=0 EndZ=0
    g8: LineSegment [constr] StartX=0 StartY=12.85 StartZ=0 EndX=0 EndY=9.85 EndZ=0
    g9: LineSegment [constr] StartX=0 StartY=3 StartZ=0 EndX=0 EndY=0 EndZ=0
  constraints (28):
    c: PointOnObject(g0,g-2)
    c: PointOnObject(g0,g-2)
    c: Vertical(g1)
    c: Coincident(g2,g0)
    c: Horizontal(g2)
    c: Coincident(g3,g0)
    c: Horizontal(g3)
    c: DistanceY(g0,g0) = 6.85
    c: Coincident(g4,g1)
    c: Horizontal(g4)
    c: Coincident(g5,g4)
    c: Coincident(g5,g2)
    c: Coincident(g6,g3)
    c: Coincident(g6,g-1)
    c: Coincident(g7,g6)
    c: Coincident(g7,g1)
    c: Horizontal(g7)
    c: DistanceY(g0,g4) = 3
    c: PointOnObject(g4,g-2)
    c: Coincident(g8,g4)
    c: Coincident(g8,g0)
    c: Coincident(g9,g0)
    c: Coincident(g9,g6)
    c: Equal(g8,g9)
    c: DistanceX(g4,g4) = 3
    c: Equal(g2,g3)
    c: DistanceX(g3,g3) = 8
    c: DistanceY(g1,g1) = 12.85
FEATURE [PartDesign::Plane] DatumPlane004
  AttachmentSupport = -> [Sketch016]
  Length = 379.502
  MapMode = 7
  Placement = pos=(-157.734,71.1614,-165.828) rot=(-0.355237,0.779497,0.515938;3.60346rad)
  ResizeMode = 0
  Width = 365.605
FEATURE [Sketcher::SketchObject] Sketch017  label="Sketch020"
  ArcFitTolerance = 1e-06
  AttachmentSupport = -> [DatumPlane004]
  ExternalTypes = [0]
  FullyConstrained = true
  MakeInternals = false
  MapMode = 5
  Placement = pos=(-157.734,71.1614,-165.828) rot=(-0.355237,0.779497,0.515938;3.60346rad)
  _ExternalGeoVersion = 0
  expr: Constraints[18] = Spreadsheet.H7 / 2 + Spreadsheet.H6
  expr: Constraints[21] = (Spreadsheet.O1 + Spreadsheet.N1) * tan(90 - 67) * 0.95
  expr: Constraints[22] = Spreadsheet.N3
  sketch-geometry (8):
    g0: LineSegment [constr] StartX=50.25 StartY=87.0356 StartZ=0 EndX=0 EndY=174.071 EndZ=0
    g1: LineSegment [constr] StartX=0 StartY=174.071 StartZ=0 EndX=-100.5 EndY=174.071 EndZ=0
    g2: LineSegment [constr] StartX=-100.5 StartY=174.071 StartZ=0 EndX=-150.75 EndY=87.0356 EndZ=0
    g3: LineSegment [constr] StartX=-150.75 StartY=87.0356 StartZ=0 EndX=-100.5 EndY=-1.42e-14 EndZ=0
    g4: LineSegment [constr] StartX=-100.5 StartY=-1.42e-14 StartZ=0 EndX=0 EndY=0 EndZ=0
    g5: LineSegment [constr] StartX=0 StartY=0 StartZ=0 EndX=50.25 EndY=87.0356 EndZ=0
    g6: Circle [constr] CenterX=-50.25 CenterY=87.0356 CenterZ=0 NormalX=0 NormalY=0 NormalZ=1 AngleXU=0 Radius=100.5
    g7: LineSegment StartX=25 StartY=43.3013 StartZ=0 EndX=-3.19576 EndY=-5.53523 EndZ=0
  constraints (20):
    c: Coincident(g0,g1)
    c: Coincident(g1,g2)
    c: Coincident(g2,g3)
    c: Coincident(g3,g4)
    c: Coincident(g4,g5)
    c: Coincident(g5,g0)
    c: Equal(g0, g1-g5) x5
    c: PointOnObject(g0,g6)
    c: PointOnObject(g1,g6)
    c: PointOnObject(g2,g6)
    c: PointOnObject(g3,g6)
    c: PointOnObject(g5,g6)
    c: Coincident(g4,g-1)
    c: Horizontal(g1)
    c: DistanceX(g1,g1) = 100.5
    c: PointOnObject(g7,g5)
    c: PointOnObject(g4,g7)
    c: Distance(g7,g-1) = 6.39153
    c: Distance(g7,g-1) = 50
    c: PointOnObject(g4,g6)
FEATURE [PartDesign::AdditivePipe] AdditivePipe001
  AuxiliaryCurvilinear = true
  AuxiliarySpineTangent = false
  BaseFeature = -> Pad008
  Binormal = (0,0,0)
  Mode = 0
  Placement = pos=(0,0,-170) rot=(0,0,1;0rad)
  Profile = -> Sketch016
  Refine = true
  Spine = -> Sketch017
  SpineTangent = false
  Suppressed = false
  Transformation = 0
  Transition = 0
FEATURE [PartDesign::Plane] DatumPlane005
  AttachmentSupport = -> [AdditivePipe001]
  Length = 367.181
  MapMode = 45
  Placement = pos=(-126.851,110.897,-167) rot=(0.255595,0.68362,0.68362;2.64112rad)
  ResizeMode = 0
  Width = 244.758
FEATURE [PartDesign::Mirrored] Mirrored
  BaseFeature = -> AdditivePipe001
  MirrorPlane = -> DatumPlane005
  Originals = -> [AdditivePipe001]
  Placement = pos=(0,0,-170) rot=(0,0,1;0rad)
  Refine = true
  Suppressed = false
  TransformMode = 0
FEATURE [PartDesign::Plane] DatumPlane006
  Length = 435.009
  MapMode = 1
  Placement = pos=(-157.73,71.16,-165.83) rot=(-0.36,0.78,0.52;3.60341rad)
  ResizeMode = 0
  Width = 386.48
FEATURE [Sketcher::SketchObject] Sketch018  label="Sketch021"
  ArcFitTolerance = 1e-06
  AttachmentSupport = -> [DatumPlane006]
  ExternalTypes = [0]
  FullyConstrained = true
  MakeInternals = false
  MapMode = 5
  Placement = pos=(-157.73,71.16,-165.83) rot=(-0.358497,0.776744,0.51783;3.60341rad)
  _ExternalGeoVersion = 0
  expr: Constraints[22] = Spreadsheet.H7
  expr: Constraints[2] = Spreadsheet.H6
  sketch-geometry (8):
    g0: LineSegment [constr] StartX=0 StartY=0 StartZ=0 EndX=-0.5 EndY=0 EndZ=0
    g1: LineSegment StartX=-0.5 StartY=0 StartZ=0 EndX=49.5 EndY=86.6025 EndZ=0
    g2: LineSegment StartX=49.5 StartY=86.6025 StartZ=0 EndX=-0.5 EndY=173.205 EndZ=0
    g3: LineSegment StartX=-0.5 StartY=173.205 StartZ=0 EndX=-100.5 EndY=173.205 EndZ=0
    g4: LineSegment StartX=-100.5 StartY=173.205 StartZ=0 EndX=-150.5 EndY=86.6025 EndZ=0
    g5: LineSegment StartX=-150.5 StartY=86.6025 StartZ=0 EndX=-100.5 EndY=0 EndZ=0
    g6: LineSegment StartX=-100.5 StartY=0 StartZ=0 EndX=-0.5 EndY=0 EndZ=0
    g7: Circle [constr] CenterX=-50.5 CenterY=86.6025 CenterZ=0 NormalX=0 NormalY=0 NormalZ=1 AngleXU=0 Radius=100
  constraints (19):
    c: Coincident(g0,g-1)
    c: Horizontal(g0)
    c: DistanceX(g0,g0) = 0.5
    c: Coincident(g1,g2)
    c: Coincident(g2,g3)
    c: Coincident(g3,g4)
    c: Coincident(g4,g5)
    c: Coincident(g5,g6)
    c: Coincident(g6,g1)
    c: Equal(g1, g2-g6) x5
    c: PointOnObject(g1,g7)
    c: PointOnObject(g2,g7)
    c: PointOnObject(g3,g7)
    c: PointOnObject(g4,g7)
    c: PointOnObject(g5,g7)
    c: PointOnObject(g6,g7)
    c: Horizontal(g6)
    c: Coincident(g1,g0)
    c: Diameter(g7) = 200
FEATURE [PartDesign::Pad] Pad009
  Direction = (-0.697931,0.602571,-0.38704)
  Length = 6.35
  Length2 = 10
  Placement = pos=(-157.73,71.16,-165.83) rot=(-0.36,0.78,0.52;3.60341rad)
  Profile = -> Sketch018
  ReferenceAxis = -> Sketch018 [N_Axis]
  Refine = true
  Reversed = true
  SideType = 0
  Suppressed = false
  Type = 0
  Type2 = 0
  expr: Length = Spreadsheet.H1
FEATURE [PartDesign::Fillet] Fillet007
  Base = -> Pad009 [Edge1,Edge14,Edge2,Edge5,Edge8,Edge11]
  BaseFeature = -> Pad009
  Placement = pos=(-157.73,71.16,-165.83) rot=(-0.36,0.78,0.52;3.60341rad)
  Radius = 1
  Refine = true
  SupportTransform = false
  Suppressed = false
  UseAllEdges = false
FEATURE [PartDesign::Body] Body006
  AllowCompound = false
  Group = -> [DatumPlane006,Sketch018,Pad009,Fillet007]
  Origin = -> Origin018
  Tip = -> Fillet007
FEATURE [PartDesign::Pocket] Pocket003
  BaseFeature = -> Mirrored
  Direction = (0,0,-1)
  Length = 5
  Length2 = 5
  Placement = pos=(0,0,-170) rot=(0,0,1;0rad)
  Profile = -> Sketch014
  ReferenceAxis = -> Sketch014 [N_Axis]
  Refine = true
  SideType = 0
  Suppressed = false
  Type = 0
  Type2 = 0
FEATURE [PartDesign::Fillet] Fillet008
  Base = -> Pocket003 [Edge8,Edge36,Edge5,Edge34,Edge76,Edge47,Edge72,Edge40,Edge38,Edge50,Edge74,Edge52,Edge51,Edge49,Edge53,Edge75,Edge77,Edge78,Edge65,Edge73,Edge69,Edge67,Edge71,Edge55,Edge57,Edge59,Edge61,Edge62]
  BaseFeature = -> Pocket003
  Placement = pos=(0,0,-170) rot=(0,0,1;0rad)
  Radius = 1
  Refine = true
  SupportTransform = false
  Suppressed = false
  UseAllEdges = false
FEATURE [PartDesign::Body] Body005
  AllowCompound = true
  Group = -> [Binder002,DatumPlane001,Sketch014,Pad008,DatumPlane002,Sketch015,DatumPlane003,Sketch016,DatumPlane004,Sketch017,AdditivePipe001,DatumPlane005,Mirrored,Pocket003,Fillet008]
  Origin = -> Origin017
  Tip = -> Fillet008
COMPONENT P11 — recipe-attached ("Mirror rails 2", modeled in this document).
Construction recipe (the document's own serialized feature program — sketch geometry with constraints, then the solid features built on it; lengths are millimeters unless a unit is written):

FEATURE [Sketcher::SketchObject] Sketch019  label="Sketch022"
  ArcFitTolerance = 1e-06
  AttachmentSupport = -> [YZ_Plane026]
  ExternalTypes = [0]
  FullyConstrained = true
  MakeInternals = false
  MapMode = 5
  Placement = pos=(0,0,0) rot=(0.57735,0.57735,0.57735;2.0944rad)
  _ExternalGeoVersion = 0
  expr: Constraints[4] = Spreadsheet.N16
  sketch-geometry (15):
    g0: LineSegment StartX=-49.5728 StartY=0 StartZ=0 EndX=-49.5728 EndY=-3 EndZ=0
    g1: LineSegment [constr] StartX=-49.5728 StartY=-3 StartZ=0 EndX=-4.57276 EndY=-3 EndZ=0
    g2: LineSegment [constr] StartX=-4.57276 StartY=-3 StartZ=0 EndX=-38.5347 EndY=-32.5227 EndZ=0
    g3: LineSegment StartX=-38.5347 StartY=-32.5227 StartZ=0 EndX=-36.5665 EndY=-34.7868 EndZ=0
    g4: LineSegment StartX=-36.5665 StartY=-34.7868 StartZ=0 EndX=0 EndY=-3 EndZ=0
    g5: LineSegment StartX=15 StartY=0 StartZ=0 EndX=-49.5728 EndY=0 EndZ=0
    g6: LineSegment StartX=0 StartY=-3 StartZ=0 EndX=15 EndY=-3 EndZ=0
    g7: LineSegment StartX=15 StartY=0 StartZ=0 EndX=15 EndY=-3 EndZ=0
    g8: LineSegment [constr] StartX=-4.57276 StartY=-3 StartZ=0 EndX=0 EndY=-3 EndZ=0
    g9: LineSegment StartX=-49.5728 StartY=-3 StartZ=0 EndX=-34.5728 EndY=-3 EndZ=0
    g10: LineSegment StartX=-38.5347 StartY=-32.5227 StartZ=0 EndX=-27.214 EndY=-22.6818 EndZ=0
    g11: LineSegment StartX=-4.57276 StartY=-3 StartZ=0 EndX=-24.9499 EndY=-20.7136 EndZ=0
    g12: LineSegment StartX=-31.5728 StartY=-3 StartZ=0 EndX=-4.57276 EndY=-3 EndZ=0
    g13: ArcOfCircle CenterX=-4.57276 CenterY=-3 CenterZ=0 NormalX=0 NormalY=0 NormalZ=1 AngleXU=0 Radius=27 StartAngle=3.14159 EndAngle=3.85718
    g14: ArcOfCircle CenterX=-4.57276 CenterY=-3 CenterZ=0 NormalX=0 NormalY=0 NormalZ=1 AngleXU=0 Radius=30 StartAngle=3.14159 EndAngle=3.85718
  constraints (42):
    c: PointOnObject(g0,g-1)
    c: Vertical(g0)
    c: Horizontal(g1)
    c: Coincident(g3,g2)
    c: Angle(g1,g2) = 0.715585
    c: Coincident(g2,g1)
    c: Coincident(g1,g0)
    c: Parallel(g2,g4)
    c: Coincident(g4,g3)
    c: Perpendicular(g3,g2)
    c: Equal(g0,g3)
    c: DistanceY(g0,g0) = 3
    c: Coincident(g5,g0)
    c: PointOnObject(g4,g-2)
    c: Coincident(g6,g4)
    c: Horizontal(g6)
    c: PointOnObject(g5,g-1)
    c: Coincident(g7,g5)
    c: Coincident(g7,g6)
    c: Vertical(g7)
    c: Coincident(g8,g1)
    c: Coincident(g8,g4)
    c: Horizontal(g8)
    c: DistanceX(g6,g6) = 15
    c: DistanceX(g1,g1) = 45
    c: Equal(g1,g2)
    c: Coincident(g9,g0)
    c: PointOnObject(g9,g1)
    c: Coincident(g10,g2)
    c: PointOnObject(g10,g2)
    c: Coincident(g11,g1)
    c: PointOnObject(g11,g2)
    c: PointOnObject(g12,g1)
    c: Coincident(g12,g1)
    c: Coincident(g13,g1)
    c: Coincident(g13,g12)
    c: Coincident(g13,g11)
    c: Coincident(g14,g1)
    c: Coincident(g14,g9)
    c: Coincident(g14,g10)
    c: DistanceX(g9,g12) = 3
    c: DistanceX(g9,g9) = 15
FEATURE [PartDesign::Pad] Pad010
  Direction = (1,0,0)
  Length = 15
  Length2 = 15
  Placement = pos=(0,0,0) rot=(1,1,1;2.0944rad)
  Profile = -> Sketch019
  ReferenceAxis = -> Sketch019 [N_Axis]
  Refine = true
  Reversed = true
  SideType = 1
  Suppressed = false
  Type = 0
  Type2 = 0
  expr: Length = Spreadsheet.E2
  expr: Length2 = Spreadsheet.E2
FEATURE [Sketcher::SketchObject] Sketch020  label="Sketch023"
  ArcFitTolerance = 1e-06
  AttachmentSupport = -> [XY_Plane026]
  ExternalGeometry = -> [Pad010]
  ExternalTypes = [0]
  FullyConstrained = true
  MakeInternals = false
  MapMode = 5
  _ExternalGeoVersion = 0
  sketch-geometry (4):
    g0: Circle CenterX=0 CenterY=9.8 CenterZ=0 NormalX=0 NormalY=0 NormalZ=1 AngleXU=0 Radius=2.2
    g1: Circle CenterX=0 CenterY=-44.3728 CenterZ=0 NormalX=0 NormalY=0 NormalZ=1 AngleXU=0 Radius=2.2
    g2: LineSegment [constr] StartX=-4e-16 StartY=12 StartZ=0 EndX=-4e-16 EndY=15 EndZ=0
    g3: LineSegment [constr] StartX=0 StartY=-46.5728 StartZ=0 EndX=0 EndY=-49.5728 EndZ=0
  constraints (13):
    c: PointOnObject(g0,g-2)
    c: PointOnObject(g1,g-2)
    c: Diameter(g0) = 4.4
    c: PointOnObject(g2,g0)
    c: Symmetric(g-3,g-3,g2)
    c: Vertical(g2)
    c: PointOnObject(g3,g1)
    c: Vertical(g3)
    c: Equal(g3,g2)
    c: DistanceY(g2,g2) = 3
    c: Equal(g0,g1)
    c: PointOnObject(g3,g-4)
    c: PointOnObject(g3,g-2)
FEATURE [PartDesign::Pocket] Pocket004
  BaseFeature = -> Pad010
  Direction = (0,0,-1)
  Length = 5
  Length2 = 5
  Placement = pos=(0,0,0) rot=(1,1,1;2.0944rad)
  Profile = -> Sketch020
  ReferenceAxis = -> Sketch020 [N_Axis]
  Refine = true
  SideType = 0
  Suppressed = false
  Type = 0
  Type2 = 0
FEATURE [PartDesign::Fillet] Fillet009
  Base = -> Pocket004 [Edge4,Edge30,Edge36,Edge37,Edge38,Edge39,Edge42,Edge40,Edge41,Edge1,Edge7,Edge35]
  BaseFeature = -> Pocket004
  Placement = pos=(0,0,0) rot=(1,1,1;2.0944rad)
  Radius = 1
  Refine = true
  SupportTransform = false
  Suppressed = false
  UseAllEdges = false
FEATURE [PartDesign::Body] Body007
  AllowCompound = true
  Group = -> [Sketch019,Pad010,Sketch020,Pocket004,Fillet009]
  Origin = -> Origin026
  Tip = -> Fillet009
FEATURE [PartDesign::Plane] DatumPlane007
  Length = 123.697
  MapMode = 1
  Placement = pos=(0,0,-3) rot=(1,0,0;0.715585rad)
  ResizeMode = 0
  Width = 164.078
  expr: .Placement.Rotation.Angle = Spreadsheet.N16
FEATURE [Sketcher::SketchObject] Sketch021  label="Sketch024"
  ArcFitTolerance = 1e-06
  AttachmentSupport = -> [DatumPlane007]
  ExternalTypes = [0]
  FullyConstrained = true
  MakeInternals = false
  MapMode = 5
  Placement = pos=(0,-2e-16,-3) rot=(1,0,0;0.715585rad)
  _ExternalGeoVersion = 0
  expr: Constraints[10] = Spreadsheet.N15
  sketch-geometry (4):
    g0: LineSegment StartX=-50 StartY=0 StartZ=0 EndX=-50 EndY=-100 EndZ=0
    g1: LineSegment StartX=-50 StartY=-100 StartZ=0 EndX=50 EndY=-100 EndZ=0
    g2: LineSegment StartX=50 StartY=-100 StartZ=0 EndX=50 EndY=0 EndZ=0
    g3: LineSegment StartX=50 StartY=0 StartZ=0 EndX=-50 EndY=0 EndZ=0
  constraints (11):
    c: Coincident(g0,g1)
    c: Coincident(g1,g2)
    c: Coincident(g2,g3)
    c: Coincident(g3,g0)
    c: Vertical(g0)
    c: Vertical(g2)
    c: Horizontal(g1)
    c: PointOnObject(g0,g-1)
    c: Equal(g3,g0)
    c: Symmetric(g0,g2,g-2)
    c: DistanceY(g0,g0) = 100
FEATURE [PartDesign::Pad] Pad011
  Direction = (0,-0.656059,0.75471)
  Length = 6.35
  Length2 = 10
  Placement = pos=(0,0,-3) rot=(1,0,0;0.715585rad)
  Profile = -> Sketch021
  ReferenceAxis = -> Sketch021 [N_Axis]
  Refine = true
  Reversed = true
  SideType = 0
  Suppressed = false
  Type = 0
  Type2 = 0
  expr: Length = Spreadsheet.H1
FEATURE [PartDesign::Body] Body008
  AllowCompound = false
  Group = -> [DatumPlane007,Sketch021,Pad011]
  Origin = -> Origin027
  Tip = -> Pad011
COMPONENT P12 — recipe-attached ("Mirror rails 3", modeled in this document).
Construction recipe (the document's own serialized feature program — sketch geometry with constraints, then the solid features built on it; lengths are millimeters unless a unit is written):

FEATURE [PartDesign::Plane] DatumPlane008
  Length = 122.812
  MapMode = 1
  Placement = pos=(0,0,0) rot=(-0.052562,0.997379,0.049714;1.78261rad)
  ResizeMode = 0
  Width = 80.6103
FEATURE [Sketcher::SketchObject] Sketch022  label="Sketch025"
  ArcFitTolerance = 1e-06
  AttachmentSupport = -> [DatumPlane008]
  ExternalTypes = [0]
  FullyConstrained = true
  MakeInternals = false
  MapMode = 5
  Placement = pos=(0,0,0) rot=(-0.052562,0.997379,0.049714;1.78261rad)
  _ExternalGeoVersion = 0
  sketch-geometry (4):
    g0: LineSegment StartX=0 StartY=3 StartZ=0 EndX=60 EndY=3 EndZ=0
    g1: LineSegment StartX=60 StartY=3 StartZ=0 EndX=60 EndY=-30 EndZ=0
    g2: LineSegment StartX=60 StartY=-30 StartZ=0 EndX=0 EndY=-30 EndZ=0
    g3: LineSegment StartX=0 StartY=-30 StartZ=0 EndX=0 EndY=3 EndZ=0
  constraints (12):
    c: Horizontal(g0)
    c: Horizontal(g2)
    c: Vertical(g1)
    c: Vertical(g3)
    c: DistanceX(g2,g2) = 60
    c: Coincident(g0,g3)
    c: Coincident(g3,g2)
    c: Coincident(g2,g1)
    c: Coincident(g1,g0)
    c: DistanceY(g1,g-1) = 30
    c: PointOnObject(g2,g-2)
    c: DistanceY(g-1,g0) = 3
FEATURE [PartDesign::Pad] Pad012
  Direction = (0.971927,0.111395,-0.207242)
  Length = 3
  Length2 = 10
  Placement = pos=(0,0,0) rot=(-0.052562,0.997379,0.049714;1.78261rad)
  Profile = -> Sketch022
  ReferenceAxis = -> Sketch022 [N_Axis]
  Refine = true
  SideType = 0
  Suppressed = false
  Type = 0
  Type2 = 0
FEATURE [Sketcher::SketchObject] Sketch023  label="Sketch026"
  ArcFitTolerance = 1e-06
  AttachmentSupport = -> [XZ_Plane029]
  ExternalGeometry = -> [Pad012]
  ExternalTypes = [0]
  FullyConstrained = true
  MakeInternals = false
  MapMode = 5
  Placement = pos=(0,0,0) rot=(1,0,0;1.5708rad)
  _ExternalGeoVersion = 0
  expr: Constraints[31] = Spreadsheet.E2
  sketch-geometry (10):
    g0: LineSegment StartX=1 StartY=0 StartZ=0 EndX=-9.83372 EndY=-59.291 EndZ=0
    g1: LineSegment StartX=-9.83372 StartY=-59.291 StartZ=0 EndX=31 EndY=-59.291 EndZ=0
    g2: LineSegment StartX=31 StartY=-59.291 StartZ=0 EndX=31 EndY=0 EndZ=0
    g3: LineSegment StartX=31 StartY=0 StartZ=0 EndX=1 EndY=0 EndZ=0
    g4: Circle CenterX=16 CenterY=-11.2 CenterZ=0 NormalX=0 NormalY=0 NormalZ=1 AngleXU=0 Radius=2.2
    g5: Circle CenterX=16 CenterY=-48.091 CenterZ=0 NormalX=0 NormalY=0 NormalZ=1 AngleXU=0 Radius=2.2
    g6: LineSegment [constr] StartX=16 StartY=-9 StartZ=0 EndX=16 EndY=0 EndZ=0
    g7: LineSegment [constr] StartX=18.2 StartY=-11.2 StartZ=0 EndX=31 EndY=-11.2 EndZ=0
    g8: LineSegment [constr] StartX=16 StartY=-50.291 StartZ=0 EndX=16 EndY=-59.291 EndZ=0
    g9: LineSegment [constr] StartX=18.2 StartY=-48.091 StartZ=0 EndX=31 EndY=-48.091 EndZ=0
  constraints (33):
    c: Coincident(g0,g1)
    c: Coincident(g1,g2)
    c: Coincident(g2,g3)
    c: Coincident(g3,g0)
    c: Vertical(g2)
    c: Horizontal(g1)
    c: Horizontal(g3)
    c: Coincident(g0,g-3)
    c: DistanceX(g3,g3) = 30
    c: Diameter(g5) = 4.4
    c: Equal(g4,g5)
    c: PointOnObject(g6,g4)
    c: PointOnObject(g6,g3)
    c: Vertical(g6)
    c: PointOnObject(g7,g4)
    c: PointOnObject(g7,g2)
    c: Horizontal(g7)
    c: PointOnObject(g8,g5)
    c: PointOnObject(g8,g1)
    c: Vertical(g8)
    c: PointOnObject(g9,g5)
    c: PointOnObject(g9,g2)
    c: Horizontal(g9)
    c: Perpendicular(g4,g6)
    c: Perpendicular(g4,g7)
    c: Perpendicular(g5,g8)
    c: Perpendicular(g5,g9)
    c: Equal(g7,g9)
    c: Equal(g8,g6)
    c: DistanceY(g6,g6) = 9
    c: DistanceX(g-1,g0) = 1
    c: Distance(g4,g2) = 15
    c: PointOnObject(g0,g-1)
FEATURE [PartDesign::Pad] Pad013
  BaseFeature = -> Pad012
  Direction = (0,-1,2e-16)
  Length = 3
  Length2 = 10
  Placement = pos=(0,0,0) rot=(-0.052562,0.997379,0.049714;1.78261rad)
  Profile = -> Sketch023
  ReferenceAxis = -> Sketch023 [N_Axis]
  Refine = true
  SideType = 0
  Suppressed = false
  Type = 0
  Type2 = 0
FEATURE [Sketcher::SketchObject] Sketch024  label="Sketch027"
  ArcFitTolerance = 1e-06
  AttachmentSupport = -> [XY_Plane029]
  ExternalGeometry = -> [Pad013]
  ExternalTypes = [0]
  FullyConstrained = true
  MakeInternals = false
  MapMode = 5
  _ExternalGeoVersion = 0
  sketch-geometry (3):
    g0: LineSegment StartX=3.30508 StartY=-29.31 StartZ=0 EndX=31 EndY=-3 EndZ=0
    g1: LineSegment StartX=3.30508 StartY=-29.31 StartZ=0 EndX=0 EndY=0 EndZ=0
    g2: LineSegment StartX=0 StartY=0 StartZ=0 EndX=31 EndY=-3 EndZ=0
  constraints (7):
    c: Coincident(g1,g-1)
    c: Coincident(g2,g1)
    c: Coincident(g2,g0)
    c: Coincident(g0,g-4)
    c: Coincident(g1,g0)
    c: PointOnObject(g0,g-3)
    c: DistanceY(g-3,g0) = 0.5
FEATURE [PartDesign::Pad] Pad014
  BaseFeature = -> Pad013
  Direction = (0,0,1)
  Length = 3
  Length2 = 0
  Placement = pos=(0,0,0) rot=(-0.052562,0.997379,0.049714;1.78261rad)
  Profile = -> Sketch024
  ReferenceAxis = -> Sketch024 [N_Axis]
  Refine = true
  Reversed = true
  SideType = 1
  Suppressed = false
  Type = 0
  Type2 = 0
FEATURE [PartDesign::Plane] DatumPlane009
  AttachmentSupport = -> [Pad014]
  Length = 77.24
  MapMode = 5
  Placement = pos=(-9.71e-14,-4.01e-14,-59.291) rot=(0.666313,0.745672,0;3.14159rad)
  ResizeMode = 0
  Width = 90.6474
FEATURE [Sketcher::SketchObject] Sketch025  label="Sketch028"
  ArcFitTolerance = 1e-06
  AttachmentSupport = -> [DatumPlane009]
  ExternalGeometry = -> [Pad014]
  ExternalTypes = [0]
  FullyConstrained = false
  MakeInternals = false
  MapMode = 5
  Placement = pos=(-9.71e-14,-4.01e-14,-59.291) rot=(0.666313,0.745672,0;3.14159rad)
  _ExternalGeoVersion = 0
  sketch-geometry (4):
    g0: LineSegment StartX=-37.8521 StartY=-23.1435 StartZ=0 EndX=19.9271 EndY=-23.1435 EndZ=0
    g1: LineSegment StartX=19.9271 StartY=-23.1435 StartZ=0 EndX=19.9271 EndY=35.7796 EndZ=0
    g2: LineSegment StartX=19.9271 StartY=35.7796 StartZ=0 EndX=-37.8521 EndY=35.7796 EndZ=0
    g3: LineSegment StartX=-37.8521 StartY=35.7796 StartZ=0 EndX=-37.8521 EndY=-23.1435 EndZ=0
  constraints (8):
    c: Coincident(g0,g1)
    c: Coincident(g1,g2)
    c: Coincident(g2,g3)
    c: Coincident(g3,g0)
    c: Horizontal(g0)
    c: Horizontal(g2)
    c: Vertical(g1)
    c: Vertical(g3)
FEATURE [PartDesign::Pocket] Pocket005
  BaseFeature = -> Pad014
  Direction = (0,0,1)
  Length = 5
  Length2 = 5
  Placement = pos=(0,0,0) rot=(-0.052562,0.997379,0.049714;1.78261rad)
  Profile = -> Sketch025
  ReferenceAxis = -> Sketch025 [N_Axis]
  Refine = true
  Reversed = true
  SideType = 0
  Suppressed = false
  Type = 0
  Type2 = 0
FEATURE [Sketcher::SketchObject] Sketch026  label="Sketch029"
  ArcFitTolerance = 1e-06
  AttachmentSupport = -> [DatumPlane009]
  ExternalGeometry = -> [Pocket005]
  ExternalTypes = [0]
  FullyConstrained = true
  MakeInternals = false
  MapMode = 5
  Placement = pos=(-9.71e-14,-4.01e-14,-59.291) rot=(0.666313,0.745672,0;3.14159rad)
  _ExternalGeoVersion = 0
  sketch-geometry (3):
    g0: LineSegment StartX=-29.49 StartY=-9.43984 StartZ=0 EndX=-6.45476 EndY=30.4686 EndZ=0
    g1: LineSegment StartX=-6.45476 StartY=30.4686 StartZ=0 EndX=-1.94888 EndY=-9.49013 EndZ=0
    g2: LineSegment StartX=-29.49 StartY=-9.43984 StartZ=0 EndX=-1.94888 EndY=-9.49013 EndZ=0
  constraints (6):
    c: Coincident(g0,g-3)
    c: Coincident(g1,g0)
    c: Coincident(g2,g0)
    c: Coincident(g2,g1)
    c: Coincident(g1,g-4)
    c: Coincident(g0,g-4)
FEATURE [PartDesign::Pad] Pad015
  BaseFeature = -> Pocket005
  Direction = (0,0,-1)
  Length = 3
  Length2 = 0
  Placement = pos=(0,0,0) rot=(-0.052562,0.997379,0.049714;1.78261rad)
  Profile = -> Sketch026
  ReferenceAxis = -> Sketch026 [N_Axis]
  Refine = true
  Reversed = true
  SideType = 0
  Suppressed = false
  Type = 0
  Type2 = 0
FEATURE [Sketcher::SketchObject] Sketch027  label="Sketch030"
  ArcFitTolerance = 1e-06
  AttachmentSupport = -> [XY_Plane029]
  ExternalTypes = [0]
  FullyConstrained = false
  MakeInternals = false
  MapMode = 5
  _ExternalGeoVersion = 0
  sketch-geometry (4):
    g0: LineSegment StartX=-27.5612 StartY=8.14378 StartZ=0 EndX=-27.5612 EndY=0 EndZ=0
    g1: LineSegment StartX=-27.5612 StartY=0 StartZ=0 EndX=13.0637 EndY=0 EndZ=0
    g2: LineSegment StartX=13.0637 StartY=0 StartZ=0 EndX=13.0637 EndY=8.14378 EndZ=0
    g3: LineSegment StartX=13.0637 StartY=8.14378 StartZ=0 EndX=-27.5612 EndY=8.14378 EndZ=0
  constraints (9):
    c: Coincident(g0,g1)
    c: Coincident(g1,g2)
    c: Coincident(g2,g3)
    c: Coincident(g3,g0)
    c: Vertical(g0)
    c: Vertical(g2)
    c: Horizontal(g1)
    c: Horizontal(g3)
    c: PointOnObject(g1,g-1)
FEATURE [PartDesign::Pocket] Pocket006
  BaseFeature = -> Pad015
  Direction = (0,0,-1)
  Length = 100
  Length2 = 100
  Placement = pos=(0,0,0) rot=(-0.052562,0.997379,0.049714;1.78261rad)
  Profile = -> Sketch027
  ReferenceAxis = -> Sketch027 [N_Axis]
  Refine = true
  Reversed = true
  SideType = 1
  Suppressed = false
  Type = 0
  Type2 = 0
FEATURE [PartDesign::Body] Body009
  AllowCompound = false
  Group = -> [DatumPlane008,Sketch022,Pad012,Sketch023,Pad013,Sketch024,Pad014,DatumPlane009,Sketch025,Pocket005,Sketch026,Pad015,Sketch027,Pocket006]
  Origin = -> Origin029
  Tip = -> Pocket006
FEATURE [Sketcher::SketchObject] Sketch028  label="Sketch031"
  ArcFitTolerance = 1e-06
  AttachmentSupport = -> [XY_Plane030]
  ExternalTypes = [0]
  FullyConstrained = true
  MakeInternals = false
  MapMode = 5
  _ExternalGeoVersion = 0
  expr: Constraints[10] = Spreadsheet.N15
  sketch-geometry (4):
    g0: LineSegment StartX=0 StartY=0 StartZ=0 EndX=0 EndY=-100 EndZ=0
    g1: LineSegment StartX=0 StartY=-100 StartZ=0 EndX=100 EndY=-100 EndZ=0
    g2: LineSegment StartX=100 StartY=-100 StartZ=0 EndX=100 EndY=0 EndZ=0
    g3: LineSegment StartX=100 StartY=0 StartZ=0 EndX=0 EndY=0 EndZ=0
  constraints (11):
    c: Coincident(g0,g1)
    c: Coincident(g1,g2)
    c: Coincident(g2,g3)
    c: Coincident(g3,g0)
    c: Vertical(g0)
    c: Vertical(g2)
    c: Horizontal(g1)
    c: Horizontal(g3)
    c: Coincident(g0,g-1)
    c: Equal(g0,g3)
    c: DistanceX(g3,g3) = 100
FEATURE [PartDesign::Pad] Pad016
  Direction = (0,0,1)
  Length = 6.35
  Length2 = 10
  Profile = -> Sketch028
  ReferenceAxis = -> Sketch028 [N_Axis]
  Refine = true
  Reversed = true
  SideType = 0
  Suppressed = false
  Type = 0
  Type2 = 0
  expr: Length = Spreadsheet.H1
FEATURE [PartDesign::Body] Body010
  AllowCompound = false
  Group = -> [Sketch028,Pad016]
  Origin = -> Origin030
  Placement = pos=(0,0,0) rot=(-0.05,1,0.049714;1.78261rad)
  Tip = -> Pad016
COMPONENT P13 — recipe-attached ("Camera", modeled in this document).
Construction recipe (the document's own serialized feature program — sketch geometry with constraints, then the solid features built on it; lengths are millimeters unless a unit is written):

FEATURE [PartDesign::Plane] DatumPlane010
  Length = 314.267
  MapMode = 1
  Placement = pos=(-5.44639,-5.45,-1.5) rot=(-0.230412,-0.551841,-0.801487;3.77945rad)
  ResizeMode = 0
  Width = 249.485
FEATURE [Sketcher::SketchObject] Sketch029  label="Sketch032"
  ArcFitTolerance = 1e-06
  AttachmentSupport = -> [DatumPlane010]
  ExternalTypes = [0]
  FullyConstrained = true
  MakeInternals = false
  MapMode = 5
  Placement = pos=(-5.44639,-5.45,-1.5) rot=(0.230412,0.551841,0.801487;2.50373rad)
  _ExternalGeoVersion = 0
  expr: Constraints[14] = Spreadsheet.B21
  expr: Constraints[15] = Spreadsheet.B24
  expr: Constraints[17] = Spreadsheet.B22 / 2
  sketch-geometry (6):
    g0: LineSegment StartX=40 StartY=80 StartZ=0 EndX=40 EndY=0 EndZ=0
    g1: LineSegment StartX=35 StartY=80 StartZ=0 EndX=35 EndY=5 EndZ=0
    g2: LineSegment StartX=35 StartY=80 StartZ=0 EndX=40 EndY=80 EndZ=0
    g3: LineSegment StartX=35 StartY=5 StartZ=0 EndX=-120 EndY=5 EndZ=0
    g4: LineSegment StartX=-120 StartY=5 StartZ=0 EndX=-120 EndY=0 EndZ=0
    g5: LineSegment StartX=-120 StartY=0 StartZ=0 EndX=40 EndY=0 EndZ=0
  constraints (18):
    c: Vertical(g0)
    c: Vertical(g1)
    c: Coincident(g2,g1)
    c: Coincident(g2,g0)
    c: Coincident(g3,g1)
    c: Horizontal(g3)
    c: Coincident(g4,g3)
    c: PointOnObject(g4,g-1)
    c: Vertical(g4)
    c: Coincident(g5,g0)
    c: Horizontal(g5)
    c: Horizontal(g2)
    c: Equal(g4,g2)
    c: DistanceX(g2,g2) = 5
    c: DistanceY(g0,g0) = 80
    c: DistanceX(g5,g5) = 160
    c: Coincident(g4,g5)
    c: Distance(g-2,g1) = 35
FEATURE [PartDesign::Pad] Pad017
  Direction = (0.661642,0.660415,0.355081)
  Length = 10
  Length2 = 5
  Placement = pos=(-5.44639,-5.45,-1.5) rot=(-0.230412,-0.551841,-0.801487;3.77945rad)
  Profile = -> Sketch029
  ReferenceAxis = -> Sketch029 [N_Axis]
  Refine = true
  SideType = 1
  Suppressed = false
  Type = 0
  Type2 = 0
  expr: Length = Spreadsheet.B23
FEATURE [Sketcher::SketchObject] Sketch030  label="Sketch033"
  ArcFitTolerance = 1e-06
  AttachmentSupport = -> [DatumPlane010]
  ExternalGeometry = -> [Pad017]
  ExternalTypes = [0]
  FullyConstrained = true
  MakeInternals = false
  MapMode = 5
  Placement = pos=(-5.44639,-5.45,-1.5) rot=(0.230412,0.551841,0.801487;2.50373rad)
  _ExternalGeoVersion = 0
  expr: Constraints[9] = Spreadsheet.B22
  sketch-geometry (74):
    g0: LineSegment [constr] StartX=-35 StartY=5 StartZ=0 EndX=-35 EndY=80 EndZ=0
    g1: LineSegment StartX=-35 StartY=80 StartZ=0 EndX=-120 EndY=80 EndZ=0
    g2: LineSegment StartX=-120 StartY=80 StartZ=0 EndX=-120 EndY=5 EndZ=0
    g3: LineSegment [constr] StartX=-35 StartY=80 StartZ=0 EndX=35 EndY=80 EndZ=0
    g4: LineSegment StartX=-35 StartY=80 StartZ=0 EndX=-35 EndY=15 EndZ=0
    g5: LineSegment StartX=-35 StartY=15 StartZ=0 EndX=25 EndY=15 EndZ=0
    g6: LineSegment StartX=35 StartY=80 StartZ=0 EndX=35 EndY=5 EndZ=0
    g7: LineSegment StartX=-120 StartY=5 StartZ=0 EndX=35 EndY=5 EndZ=0
    g8: LineSegment [constr] StartX=-113 StartY=73 StartZ=0 EndX=-113 EndY=15 EndZ=0
    g9: LineSegment [constr] StartX=-113 StartY=15 StartZ=0 EndX=-42 EndY=15 EndZ=0
    g10: LineSegment [constr] StartX=-42 StartY=15 StartZ=0 EndX=-42 EndY=73 EndZ=0
    g11: LineSegment [constr] StartX=-42 StartY=73 StartZ=0 EndX=-113 EndY=73 EndZ=0
    g12: LineSegment [constr] StartX=-113 StartY=73 StartZ=0 EndX=-113 EndY=80 EndZ=0
    g13: LineSegment [constr] StartX=-113 StartY=73 StartZ=0 EndX=-120 EndY=73 EndZ=0
    g14: LineSegment [constr] StartX=-42 StartY=15 StartZ=0 EndX=-35 EndY=15 EndZ=0
    g15: LineSegment [constr] StartX=-77.5 StartY=73 StartZ=0 EndX=-77.5 EndY=15 EndZ=0
    g16: LineSegment [constr] StartX=-113 StartY=44 StartZ=0 EndX=-42 EndY=44 EndZ=0
    g17: GeomPoint [constr] X=-77.5 Y=44 Z=0
    g18: LineSegment [constr] StartX=-86.6437 StartY=73 StartZ=0 EndX=-68.3563 EndY=15 EndZ=0
    g19: LineSegment [constr] StartX=-86.6437 StartY=15 StartZ=0 EndX=-68.3563 EndY=73 EndZ=0
    g20: LineSegment [constr] StartX=-42 StartY=55.1931 StartZ=0 EndX=-113 EndY=32.8069 EndZ=0
    g21: LineSegment [constr] StartX=-113 StartY=55.1931 StartZ=0 EndX=-42 EndY=32.8069 EndZ=0
    g22: Circle [constr] CenterX=-77.5 CenterY=44 CenterZ=0 NormalX=0 NormalY=0 NormalZ=1 AngleXU=0 Radius=9
    g23: Circle CenterX=-77.5 CenterY=44 CenterZ=0 NormalX=0 NormalY=0 NormalZ=1 AngleXU=0 Radius=6.5
    g24: ArcOfCircle CenterX=-77.5 CenterY=44 CenterZ=0 NormalX=0 NormalY=0 NormalZ=1 AngleXU=0 Radius=9 StartAngle=1.26536 EndAngle=1.87623
    g25: ArcOfCircle CenterX=-77.5 CenterY=44 CenterZ=0 NormalX=0 NormalY=0 NormalZ=1 AngleXU=0 Radius=9 StartAngle=5.97775 EndAngle=6.58862
    g26: ArcOfCircle CenterX=-77.5 CenterY=44 CenterZ=0 NormalX=0 NormalY=0 NormalZ=1 AngleXU=0 Radius=9 StartAngle=4.40696 EndAngle=5.01782
    g27: ArcOfCircle CenterX=-77.5 CenterY=44 CenterZ=0 NormalX=0 NormalY=0 NormalZ=1 AngleXU=0 Radius=9 StartAngle=2.83616 EndAngle=3.44703
    g28: LineSegment [constr] StartX=-80.2064 StartY=52.5835 StartZ=0 EndX=-74.7936 EndY=52.5835 EndZ=0
    g29: LineSegment [constr] StartX=-68.9165 StartY=46.7064 StartZ=0 EndX=-68.9165 EndY=41.2936 EndZ=0
    g30: LineSegment StartX=-74.7936 StartY=52.5835 StartZ=0 EndX=-68.3563 EndY=73 EndZ=0
    g31: LineSegment StartX=-80.2064 StartY=52.5835 StartZ=0 EndX=-86.6437 EndY=73 EndZ=0
    g32: LineSegment StartX=-86.6437 StartY=73 StartZ=0 EndX=-68.3563 EndY=73 EndZ=0
    g33: LineSegment StartX=-68.9165 StartY=46.7064 StartZ=0 EndX=-42 EndY=55.1931 EndZ=0
    g34: LineSegment StartX=-68.9165 StartY=41.2936 StartZ=0 EndX=-42 EndY=32.8069 EndZ=0
    g35: LineSegment StartX=-42 StartY=32.8069 StartZ=0 EndX=-42 EndY=55.1931 EndZ=0
    g36: LineSegment StartX=-80.2064 StartY=35.4165 StartZ=0 EndX=-86.6437 EndY=15 EndZ=0
    g37: LineSegment StartX=-86.6437 StartY=15 StartZ=0 EndX=-68.3563 EndY=15 EndZ=0
    g38: LineSegment StartX=-68.3563 StartY=15 StartZ=0 EndX=-74.7936 EndY=35.4165 EndZ=0
    g39: LineSegment StartX=-86.0835 StartY=46.7064 StartZ=0 EndX=-113 EndY=55.1931 EndZ=0
    g40: LineSegment StartX=-113 StartY=55.1931 StartZ=0 EndX=-113 EndY=32.8069 EndZ=0
    g41: LineSegment StartX=-113 StartY=32.8069 StartZ=0 EndX=-86.0835 EndY=41.2936 EndZ=0
    g42: LineSegment [constr] StartX=-92.5964 StartY=73 StartZ=0 EndX=-62.4036 EndY=15 EndZ=0
    g43: LineSegment [constr] StartX=-92.5964 StartY=15 StartZ=0 EndX=-62.4036 EndY=73 EndZ=0
    g44: LineSegment [constr] StartX=-113 StartY=62.4801 StartZ=0 EndX=-42 EndY=25.5199 EndZ=0
    g45: LineSegment [constr] StartX=-42 StartY=62.4801 StartZ=0 EndX=-113 EndY=25.5199 EndZ=0
    g46: ArcOfCircle CenterX=-77.5 CenterY=44 CenterZ=0 NormalX=0 NormalY=0 NormalZ=1 AngleXU=0 Radius=9 StartAngle=0.479966 EndAngle=1.09083
    g47: ArcOfCircle CenterX=-77.5 CenterY=44 CenterZ=0 NormalX=0 NormalY=0 NormalZ=1 AngleXU=0 Radius=9 StartAngle=5.19235 EndAngle=5.80322
    g48: ArcOfCircle CenterX=-77.5 CenterY=44 CenterZ=0 NormalX=0 NormalY=0 NormalZ=1 AngleXU=0 Radius=9 StartAngle=3.62156 EndAngle=4.23242
    g49: ArcOfCircle CenterX=-77.5 CenterY=44 CenterZ=0 NormalX=0 NormalY=0 NormalZ=1 AngleXU=0 Radius=9 StartAngle=2.05076 EndAngle=2.66163
    g50: LineSegment [constr] StartX=-73.3443 StartY=51.9831 StartZ=0 EndX=-69.5169 EndY=48.1557 EndZ=0
    g51: LineSegment [constr] StartX=-69.5169 StartY=39.8443 StartZ=0 EndX=-73.3443 EndY=36.0169 EndZ=0
    g52: LineSegment [constr] StartX=-69.5169 StartY=39.8443 StartZ=0 EndX=-68.9165 EndY=41.2936 EndZ=0
    g53: LineSegment [constr] StartX=-73.3443 StartY=36.0169 StartZ=0 EndX=-74.7936 EndY=35.4165 EndZ=0
    g54: LineSegment [constr] StartX=-74.7936 StartY=52.5835 StartZ=0 EndX=-73.3443 EndY=51.9831 EndZ=0
    g55: LineSegment [constr] StartX=-69.5169 StartY=48.1557 StartZ=0 EndX=-68.9165 EndY=46.7064 EndZ=0
    g56: LineSegment StartX=-85.4831 StartY=39.8443 StartZ=0 EndX=-113 EndY=25.5199 EndZ=0
    g57: LineSegment StartX=-81.6557 StartY=36.0169 StartZ=0 EndX=-92.5964 EndY=15 EndZ=0
    g58: LineSegment StartX=-92.5964 StartY=15 StartZ=0 EndX=-113 EndY=15 EndZ=0
    g59: LineSegment StartX=-113 StartY=15 StartZ=0 EndX=-113 EndY=25.5199 EndZ=0
    g60: LineSegment StartX=-73.3443 StartY=36.0169 StartZ=0 EndX=-62.4036 EndY=15 EndZ=0
    g61: LineSegment StartX=-62.4036 StartY=15 StartZ=0 EndX=-42 EndY=15 EndZ=0
    g62: LineSegment StartX=-42 StartY=15 StartZ=0 EndX=-42 EndY=25.5199 EndZ=0
    g63: LineSegment StartX=-42 StartY=25.5199 StartZ=0 EndX=-69.5169 EndY=39.8443 EndZ=0
    g64: LineSegment StartX=-73.3443 StartY=51.9831 StartZ=0 EndX=-62.4036 EndY=73 EndZ=0
    g65: LineSegment StartX=-62.4036 StartY=73 StartZ=0 EndX=-42 EndY=73 EndZ=0
    g66: LineSegment StartX=-42 StartY=73 StartZ=0 EndX=-42 EndY=62.4801 EndZ=0
    g67: LineSegment StartX=-42 StartY=62.4801 StartZ=0 EndX=-69.5169 EndY=48.1557 EndZ=0
    g68: LineSegment StartX=-81.6557 StartY=51.9831 StartZ=0 EndX=-92.5964 EndY=73 EndZ=0
    g69: LineSegment StartX=-92.5964 StartY=73 StartZ=0 EndX=-113 EndY=73 EndZ=0
    g70: LineSegment StartX=-113 StartY=73 StartZ=0 EndX=-113 EndY=62.4801 EndZ=0
    g71: LineSegment StartX=-113 StartY=62.4801 StartZ=0 EndX=-85.4831 EndY=48.1557 EndZ=0
    g72: LineSegment StartX=25 StartY=15 StartZ=0 EndX=25 EndY=80 EndZ=0
    g73: LineSegment StartX=25 StartY=80 StartZ=0 EndX=35 EndY=80 EndZ=0
  constraints (190):
    c: PointOnObject(g0,g-3)
    c: Vertical(g0)
    c: Coincident(g1,g0)
    c: Horizontal(g1)
    c: Coincident(g2,g1)
    c: Vertical(g2)
    c: Coincident(g3,g0)
    c: Coincident(g3,g-4)
    c: Horizontal(g3)
    c: DistanceX(g3,g3) = 70
    c: Coincident(g4,g0)
    c: PointOnObject(g4,g0)
    c: Coincident(g5,g4)
    c: Horizontal(g5)
    c: Coincident(g6,g-5)
    c: Coincident(g7,g2)
    c: Coincident(g7,g6)
    c: Coincident(g8,g9)
    c: Coincident(g9,g10)
    c: Coincident(g10,g11)
    c: Coincident(g11,g8)
    c: Vertical(g8)
    c: Vertical(g10)
    c: Horizontal(g11)
    c: Tangent(g9,g5)
    c: Coincident(g12,g8)
    c: PointOnObject(g12,g1)
    c: Vertical(g12)
    c: Coincident(g13,g8)
    c: PointOnObject(g13,g2)
    c: Horizontal(g13)
    c: Equal(g12,g13)
    c: Coincident(g2,g-3)
    c: Coincident(g14,g9)
    c: Coincident(g14,g4)
    c: Equal(g12,g14)
    c: Symmetric(g11,g11,g15)
    c: Symmetric(g9,g9,g15)
    c: Symmetric(g8,g8,g16)
    c: Symmetric(g10,g10,g16)
    c: Symmetric(g15,g15,g17)
    c: PointOnObject(g18,g11)
    c: PointOnObject(g18,g9)
    c: PointOnObject(g19,g9)
    c: PointOnObject(g19,g11)
    c: PointOnObject(g20,g10)
    c: PointOnObject(g20,g8)
    c: PointOnObject(g21,g8)
    c: PointOnObject(g17,g21)
    c: PointOnObject(g17,g19)
    c: PointOnObject(g17,g18)
    c: PointOnObject(g17,g20)
    c: PointOnObject(g21,g10)
    c: Diameter(g22) = 18
    c: Coincident(g22,g17)
    c: Diameter(g23) = 13
    c: Coincident(g23,g17)
    c: Coincident(g24,g17)
    c: PointOnObject(g24,g18)
    c: PointOnObject(g24,g19)
    c: Coincident(g25,g17)
    c: PointOnObject(g25,g20)
    c: PointOnObject(g25,g21)
    c: Coincident(g26,g17)
    c: PointOnObject(g26,g19)
    c: PointOnObject(g26,g18)
    c: Coincident(g27,g17)
    c: PointOnObject(g27,g21)
    c: PointOnObject(g27,g20)
    c: PointOnObject(g24,g22)
    c: PointOnObject(g25,g22)
    c: PointOnObject(g26,g22)
    c: PointOnObject(g27,g22)
    c: Coincident(g28,g24)
    c: Coincident(g28,g24)
    c: Horizontal(g28)
    c: Coincident(g29,g25)
    c: Coincident(g29,g25)
    c: Vertical(g29)
    c: Equal(g28,g29)
    c: Coincident(g30,g24)
    c: Coincident(g30,g19)
    c: Coincident(g31,g24)
    c: Coincident(g31,g18)
    c: Coincident(g32,g18)
    c: Coincident(g32,g30)
    c: Coincident(g33,g25)
    c: Coincident(g33,g20)
    c: Coincident(g34,g25)
    c: Coincident(g34,g21)
    c: Coincident(g35,g21)
    c: Coincident(g35,g20)
    c: Coincident(g36,g26)
    c: Coincident(g36,g19)
    c: Coincident(g37,g18)
    c: Coincident(g38,g18)
    c: Coincident(g39,g27)
    c: Coincident(g39,g21)
    c: Coincident(g40,g21)
    c: Coincident(g40,g20)
    c: Coincident(g41,g20)
    c: Coincident(g41,g27)
    c: PointOnObject(g42,g11)
    c: PointOnObject(g42,g9)
    c: PointOnObject(g43,g9)
    c: PointOnObject(g43,g11)
    c: PointOnObject(g17,g43)
    c: PointOnObject(g17,g42)
    c: PointOnObject(g17,g44)
    c: PointOnObject(g17,g45)
    c: Coincident(g46,g17)
    c: PointOnObject(g46,g43)
    c: PointOnObject(g46,g45)
    c: Coincident(g47,g17)
    c: PointOnObject(g47,g44)
    c: PointOnObject(g47,g42)
    c: Coincident(g48,g17)
    c: PointOnObject(g48,g43)
    c: PointOnObject(g48,g45)
    c: Coincident(g49,g17)
    c: PointOnObject(g49,g42)
    c: PointOnObject(g49,g44)
    c: Equal(g49,g22)
    c: Equal(g46,g22)
    c: Equal(g47,g22)
    c: Equal(g22,g48)
    c: Coincident(g50,g46)
    c: Coincident(g50,g46)
    c: Coincident(g51,g47)
    c: Coincident(g51,g47)
    c: Equal(g28,g50)
    c: Equal(g28,g51)
    c: Coincident(g38,g26)
    c: Angle(g30,g31) = 0.610865
    c: Coincident(g52,g47)
    c: Coincident(g52,g25)
    c: Coincident(g53,g47)
    c: Coincident(g53,g26)
    c: Equal(g53,g52)
    c: PointOnObject(g44,g10)
    c: PointOnObject(g44,g8)
    c: PointOnObject(g45,g8)
    c: PointOnObject(g45,g10)
    c: Coincident(g54,g24)
    c: Coincident(g54,g46)
    c: Coincident(g46,g55)
    c: Coincident(g55,g25)
    c: Equal(g54,g55)
    c: Coincident(g56,g48)
    c: Coincident(g56,g45)
    c: Coincident(g57,g48)
    c: Coincident(g57,g43)
    c: Coincident(g58,g43)
    c: Coincident(g58,g8)
    c: Coincident(g59,g8)
    c: Coincident(g59,g45)
    c: Coincident(g37,g19)
    c: Coincident(g60,g47)
    c: Coincident(g60,g42)
    c: Coincident(g61,g42)
    c: Coincident(g61,g9)
    c: Coincident(g62,g9)
    c: Coincident(g62,g44)
    c: Coincident(g63,g44)
    c: Coincident(g63,g47)
    c: Coincident(g64,g46)
    c: Coincident(g64,g43)
    c: Coincident(g65,g43)
    c: Coincident(g65,g10)
    c: Coincident(g66,g10)
    c: Coincident(g66,g45)
    c: Coincident(g67,g45)
    c: Coincident(g67,g46)
    c: Coincident(g68,g49)
    c: Coincident(g68,g42)
    c: Coincident(g69,g42)
    c: Coincident(g69,g8)
    c: Coincident(g70,g8)
    c: Coincident(g70,g44)
    c: Coincident(g71,g44)
    c: Coincident(g71,g49)
    c: DistanceX(g14,g14) = 7
    c: Coincident(g72,g5)
    c: PointOnObject(g72,g3)
    c: Vertical(g72)
    c: Coincident(g73,g72)
    c: Coincident(g73,g3)
    c: Distance(g7,g5) = 10
    c: Coincident(g6,g3)
    c: DistanceX(g73,g73) = 10
FEATURE [PartDesign::Pad] Pad018
  BaseFeature = -> Pad017
  Direction = (0.661642,0.660415,0.355081)
  Length = 5
  Length2 = 10
  Placement = pos=(-5.44639,-5.45,-1.5) rot=(-0.230412,-0.551841,-0.801487;3.77945rad)
  Profile = -> Sketch030
  ReferenceAxis = -> Sketch030 [N_Axis]
  Refine = true
  Reversed = true
  SideType = 0
  Suppressed = false
  Type = 0
  Type2 = 0
FEATURE [Sketcher::SketchObject] Sketch031  label="Sketch034"
  ArcFitTolerance = 1e-06
  AttachmentSupport = -> [XY_Plane032]
  ExternalTypes = [0]
  FullyConstrained = true
  MakeInternals = false
  MapMode = 5
  _ExternalGeoVersion = 0
  expr: Constraints[9] = Spreadsheet.E1
  sketch-geometry (13):
    g0: LineSegment StartX=0 StartY=60 StartZ=0 EndX=-30 EndY=60 EndZ=0
    g1: LineSegment StartX=-30 StartY=60 StartZ=0 EndX=-30 EndY=15.8579 EndZ=0
    g2: LineSegment StartX=15.8579 StartY=-30 StartZ=0 EndX=60 EndY=-30 EndZ=0
    g3: LineSegment StartX=60 StartY=-30 StartZ=0 EndX=60 EndY=0 EndZ=0
    g4: Circle CenterX=45 CenterY=-15 CenterZ=0 NormalX=0 NormalY=0 NormalZ=1 AngleXU=0 Radius=2.2
    g5: Circle CenterX=-15 CenterY=45 CenterZ=0 NormalX=0 NormalY=0 NormalZ=1 AngleXU=0 Radius=2.2
    g6: LineSegment [constr] StartX=-15 StartY=47.2 StartZ=0 EndX=-15 EndY=60 EndZ=0
    g7: LineSegment [constr] StartX=47.2 StartY=-15 StartZ=0 EndX=60 EndY=-15 EndZ=0
    g8: LineSegment [constr] StartX=-30 StartY=45 StartZ=0 EndX=-17.2 EndY=45 EndZ=0
    g9: ArcOfCircle CenterX=5 CenterY=5 CenterZ=0 NormalX=0 NormalY=0 NormalZ=1 AngleXU=0 Radius=5 StartAngle=3.14159 EndAngle=4.71239
    g10: LineSegment StartX=5 StartY=0 StartZ=0 EndX=60 EndY=0 EndZ=0
    g11: LineSegment StartX=0 StartY=5 StartZ=0 EndX=0 EndY=60 EndZ=0
    g12: LineSegment StartX=-30 StartY=15.8579 StartZ=0 EndX=15.8579 EndY=-30 EndZ=0
  constraints (39):
    c: PointOnObject(g0,g-2)
    c: Horizontal(g0)
    c: Vertical(g1)
    c: Horizontal(g2)
    c: Coincident(g3,g2)
    c: PointOnObject(g3,g-1)
    c: Vertical(g3)
    c: Coincident(g1,g0)
    c: Equal(g0,g3)
    c: DistanceX(g0,g0) = 30
    c: Diameter(g4) = 4.4
    c: Equal(g5,g4)
    c: PointOnObject(g6,g5)
    c: Symmetric(g0,g0,g6)
    c: Vertical(g6)
    c: PointOnObject(g7,g4)
    c: Horizontal(g7)
    c: Perpendicular(g4,g7)
    c: Perpendicular(g5,g6)
    c: Equal(g6,g7)
    c: Symmetric(g3,g2,g7)
    c: PointOnObject(g8,g1)
    c: PointOnObject(g8,g5)
    c: Horizontal(g8)
    c: Perpendicular(g5,g8)
    c: Equal(g6,g8)
    c: Coincident(g10,g3)
    c: Coincident(g11,g0)
    c: Vertical(g11)
    c: Horizontal(g10)
    c: Tangent(g10,g9) = -1.5708
    c: Tangent(g11,g9) = 1.5708
    c: Coincident(g12,g1)
    c: Coincident(g12,g2)
    c: Radius(g9) = 5
    c: Equal(g1,g2)
    c: Distance(g2,g-2) = 60
    c: Equal(g11,g10)
    c: Distance(g-1,g12) = 10
FEATURE [PartDesign::Pad] Pad019
  BaseFeature = -> Pad018
  Direction = (0,0,1)
  Length = 3
  Length2 = 10
  Placement = pos=(-5.44639,-5.45,-1.5) rot=(-0.230412,-0.551841,-0.801487;3.77945rad)
  Profile = -> Sketch031
  ReferenceAxis = -> Sketch031 [N_Axis]
  Refine = true
  SideType = 0
  Suppressed = false
  Type = 0
  Type2 = 0
FEATURE [Sketcher::SketchObject] Sketch032  label="Sketch035"
  ArcFitTolerance = 1e-06
  AttachmentSupport = -> [XY_Plane032]
  ExternalTypes = [0]
  FullyConstrained = false
  MakeInternals = false
  MapMode = 5
  _ExternalGeoVersion = 0
  sketch-geometry (4):
    g0: LineSegment StartX=-84.8731 StartY=80.5615 StartZ=0 EndX=-84.8731 EndY=-128.472 EndZ=0
    g1: LineSegment StartX=-84.8731 StartY=-128.472 StartZ=0 EndX=133.133 EndY=-128.472 EndZ=0
    g2: LineSegment StartX=133.133 StartY=-128.472 StartZ=0 EndX=133.133 EndY=80.5615 EndZ=0
    g3: LineSegment StartX=133.133 StartY=80.5615 StartZ=0 EndX=-84.8731 EndY=80.5615 EndZ=0
  constraints (8):
    c: Coincident(g0,g1)
    c: Coincident(g1,g2)
    c: Coincident(g2,g3)
    c: Coincident(g3,g0)
    c: Vertical(g0)
    c: Vertical(g2)
    c: Horizontal(g1)
    c: Horizontal(g3)
FEATURE [PartDesign::Pocket] Pocket007
  BaseFeature = -> Pad019
  Direction = (0,0,-1)
  Length = 100
  Length2 = 5
  Placement = pos=(-5.44639,-5.45,-1.5) rot=(-0.230412,-0.551841,-0.801487;3.77945rad)
  Profile = -> Sketch032
  ReferenceAxis = -> Sketch032 [N_Axis]
  Refine = true
  SideType = 0
  Suppressed = false
  Type = 0
  Type2 = 0
FEATURE [PartDesign::Fillet] Fillet010
  Base = -> Pocket007 [Edge171,Edge137,Edge138,Edge128,Edge132,Edge156,Edge112,Edge122,Edge146,Edge163,Edge154,Edge164,Edge153,Edge145,Edge148,Edge110,Edge107,Edge120,Edge117,Edge127,Edge150,Edge160,Edge114,Edge172,Edge158,Edge108,Edge118,Edge134,Edge142,Edge176,Edge178,Edge168,Edge140,Edge174,Edge166]
  BaseFeature = -> Pocket007
  Placement = pos=(-5.44639,-5.45,-1.5) rot=(-0.230412,-0.551841,-0.801487;3.77945rad)
  Radius = 1
  Refine = true
  SupportTransform = false
  Suppressed = false
  UseAllEdges = false
FEATURE [PartDesign::Fillet] Fillet011
  Base = -> Fillet010 [Edge102,Edge131,Edge108,Edge106,Edge272,Edge119,Edge271,Edge274,Edge120,Edge277,Edge280,Edge123,Edge281,Edge124,Edge111,Edge269,Edge112]
  BaseFeature = -> Fillet010
  Placement = pos=(-5.44639,-5.45,-1.5) rot=(-0.230412,-0.551841,-0.801487;3.77945rad)
  Radius = 1
  Refine = true
  SupportTransform = false
  Suppressed = false
  UseAllEdges = false
FEATURE [PartDesign::Fillet] Fillet012
  Base = -> Fillet011 [Edge277,Edge278,Edge288,Edge91,Edge88]
  BaseFeature = -> Fillet011
  Placement = pos=(-5.44639,-5.45,-1.5) rot=(-0.230412,-0.551841,-0.801487;3.77945rad)
  Radius = 3
  Refine = true
  SupportTransform = false
  Suppressed = false
  UseAllEdges = false
FEATURE [PartDesign::Body] Body011
  AllowCompound = false
  Group = -> [DatumPlane010,Sketch029,Pad017,Sketch030,Pad018,Sketch031,Pad019,Sketch032,Pocket007,Fillet010,Fillet011,Fillet012]
  Origin = -> Origin032
  Tip = -> Fillet012
PROVENANCE & LICENSES
A FreeCAD (.FCStd) document from a public repository crawl; recipes are the document's own serialized feature recipes (and, for linked parts, companion documents' recipes).
License: gpl-3.0.
